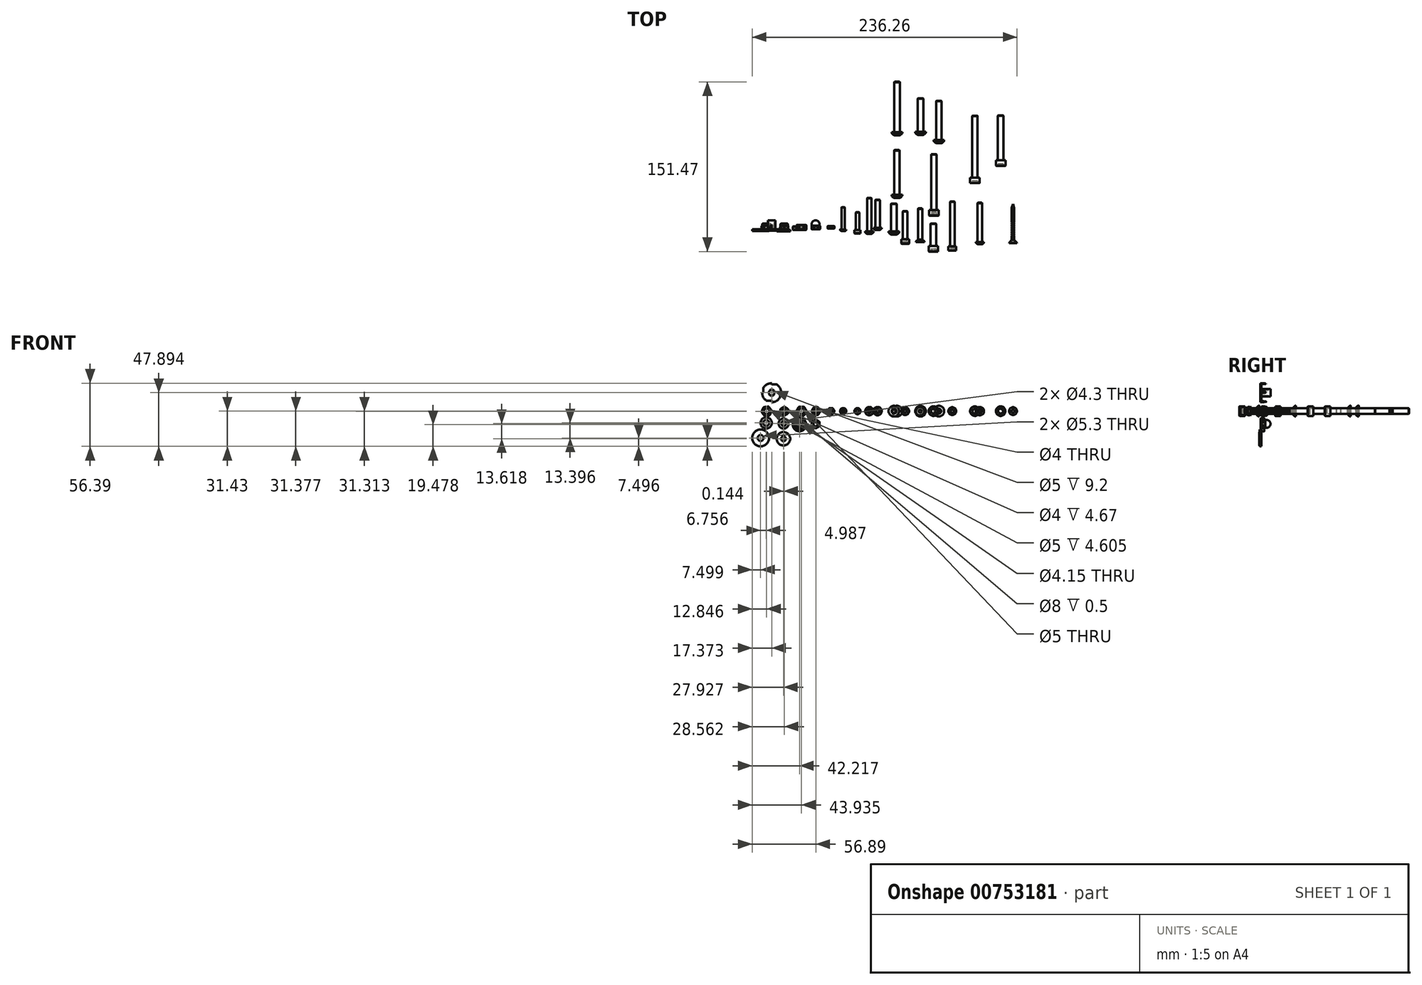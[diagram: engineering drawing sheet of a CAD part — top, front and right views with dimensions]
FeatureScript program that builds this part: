
annotation { "Feature Type Name" : "Feature", "Feature Type Description" : "" }
export const myFeature = defineFeature(function(context is Context, id is Id, definition is map)
    precondition{}
    {
        {
            var Q0;
            Q0=qCreatedBy(makeId("Top.planeOp"),FACE);
            var sketch = newSketch(context, id + "F0", { "sketchPlane" : qUnion([Q0])});
            skLineSegment(sketch, "E0.bottom", {"start": v(-2, 0) * mm, "end": v(-3.83, 0) * mm});
            skLineSegment(sketch, "E0.top", {"start": v(-2, 3) * mm, "end": v(-3.83, 3) * mm});
            skLineSegment(sketch, "E0.left", {"start": v(-2, 0) * mm, "end": v(-2, 3) * mm});
            skLineSegment(sketch, "E0.right", {"start": v(-3.83, 0) * mm, "end": v(-3.83, 3) * mm});
            skLineSegment(sketch, "E1", {"start": v(-2, 0) * mm, "end": v(0, 0) * mm, "construction": true});
            skLineSegment(sketch, "E2", {"start": v(0, 0) * mm, "end": v(0, 3) * mm, "construction": true});
            skSolve(sketch);
        }
        {
            var Q0;
            Q0=qSketchRegion(id+"F0",true);
            var Q1;
            Q1=sQuery(id+"F0.wireOp",EDGE,"E2");
            revolve(context, id + "F1", {"entities" : qUnion([Q0]), "axis" : qUnion([Q1]), "revolveType" : RevolveType.FULL});
        }
        {
            var Q0;
            Q0=makeQuery(id+"F1.opRevolve","SWEPT_EDGE",EDGE,{"disambiguationData":[OSD([sQuery(id+"F0.wireOp",EDGE,"E0.bottom"),sQuery(id+"F0.wireOp",EDGE,"E0.right")])]});
            var Q1;
            Q1=makeQuery(id+"F1.opRevolve","SWEPT_EDGE",EDGE,{"disambiguationData":[OSD([sQuery(id+"F0.wireOp",EDGE,"E0.top"),sQuery(id+"F0.wireOp",EDGE,"E0.right")])]});
            var Q2;
            Q2=makeQuery(id+"F1.opRevolve","SWEPT_EDGE",EDGE,{"disambiguationData":[OSD([sQuery(id+"F0.wireOp",EDGE,"E0.bottom"),sQuery(id+"F0.wireOp",EDGE,"E0.left")])]});
            var Q3;
            Q3=makeQuery(id+"F1.opRevolve","SWEPT_EDGE",EDGE,{"disambiguationData":[OSD([sQuery(id+"F0.wireOp",EDGE,"E0.top"),sQuery(id+"F0.wireOp",EDGE,"E0.left")])]});
            chamfer(context, id + "F2", {"entities" : qUnion([Q0, Q1, Q2, Q3]), "chamferType" : ChamferType.OFFSET_ANGLE, "width" : 0.77 * mm / 2, "oppositeDirection" : false, "angle" : 30 * degree, "tangentPropagation" : true});
        }
        {
            var Q0;
            Q0=makeQuery(id+"F1.opRevolve","SWEPT_FACE",FACE,{"disambiguationData":[OSD([sQuery(id+"F0.wireOp",EDGE,"E0.bottom")])]});
            var sketch = newSketch(context, id + "F3", { "sketchPlane" : qUnion([Q0])});
            skCircle(sketch, "E3.cCircle", {"center": v(0, 0) * mm, "radius": 3.45 * mm, "construction": true});
            skLineSegment(sketch, "E3.0", {"start": v(3.98, 0) * mm, "end": v(2, -3.45) * mm});
            skLineSegment(sketch, "E3.1", {"start": v(2, -3.45) * mm, "end": v(-2, -3.45) * mm});
            skLineSegment(sketch, "E3.2", {"start": v(-2, -3.45) * mm, "end": v(-3.98, 0) * mm});
            skLineSegment(sketch, "E3.3", {"start": v(-3.98, 0) * mm, "end": v(-2, 3.45) * mm});
            skLineSegment(sketch, "E3.4", {"start": v(-2, 3.45) * mm, "end": v(2, 3.45) * mm});
            skLineSegment(sketch, "E3.5", {"start": v(2, 3.45) * mm, "end": v(3.98, 0) * mm});
            skPoint(sketch, "E3.0.midPoint", {"position": v(2.99, -1.73) * mm});
            skCircle(sketch, "E4", {"center": v(0, 0) * mm, "radius": 4.53 * mm});
            skSolve(sketch);
        }
        {
            var Q0;
            Q0=qSketchRegion(id+"F3",true);
            extrude(context, id + "F4", {"entities" : qUnion([Q0]), "operationType" : NewBodyOperationType.REMOVE, "oppositeDirection" : true, "depth" : 25 * mm, "offsetDistance" : 25 * mm});
        }
        {
            var Q0;
            Q0=qCreatedBy(makeId("Top.planeOp"),FACE);
            var sketch = newSketch(context, id + "F5", { "sketchPlane" : qUnion([Q0])});
            skLineSegment(sketch, "E5.bottom", {"start": v(10.4, 2.85) * mm, "end": v(11.9, 2.85) * mm});
            skLineSegment(sketch, "E5.top", {"start": v(10.4, 0.58) * mm, "end": v(11.9, 0.58) * mm});
            skLineSegment(sketch, "E5.left", {"start": v(10.4, 2.85) * mm, "end": v(10.4, 0.58) * mm});
            skLineSegment(sketch, "E5.right", {"start": v(11.9, 2.85) * mm, "end": v(11.9, 0.58) * mm});
            skLineSegment(sketch, "E6", {"start": v(11.9, 0.58) * mm, "end": v(13.4, 0.58) * mm, "construction": true});
            skLineSegment(sketch, "E7", {"start": v(13.4, 0.58) * mm, "end": v(13.4, 2.85) * mm, "construction": true});
            skSolve(sketch);
        }
        {
            var Q0;
            Q0=qSketchRegion(id+"F5",true);
            var Q1;
            Q1=sQuery(id+"F5.wireOp",EDGE,"E7");
            revolve(context, id + "F6", {"entities" : qUnion([Q0]), "axis" : qUnion([Q1]), "revolveType" : RevolveType.FULL});
        }
        {
            var Q0;
            Q0=makeQuery(id+"F6.opRevolve","SWEPT_EDGE",EDGE,{"disambiguationData":[OSD([sQuery(id+"F5.wireOp",EDGE,"E5.top"),sQuery(id+"F5.wireOp",EDGE,"E5.right")])]});
            var Q1;
            Q1=makeQuery(id+"F6.opRevolve","SWEPT_EDGE",EDGE,{"disambiguationData":[OSD([sQuery(id+"F5.wireOp",EDGE,"E5.top"),sQuery(id+"F5.wireOp",EDGE,"E5.left")])]});
            var Q2;
            Q2=makeQuery(id+"F6.opRevolve","SWEPT_EDGE",EDGE,{"disambiguationData":[OSD([sQuery(id+"F5.wireOp",EDGE,"E5.bottom"),sQuery(id+"F5.wireOp",EDGE,"E5.right")])]});
            var Q3;
            Q3=makeQuery(id+"F6.opRevolve","SWEPT_EDGE",EDGE,{"disambiguationData":[OSD([sQuery(id+"F5.wireOp",EDGE,"E5.bottom"),sQuery(id+"F5.wireOp",EDGE,"E5.left")])]});
            chamfer(context, id + "F7", {"entities" : qUnion([Q0, Q1, Q2, Q3]), "width" : 0.51 / 2 * mm, "tangentPropagation" : true});
        }
        {
            var Q0;
            Q0=makeQuery(id+"F6.opRevolve","SWEPT_FACE",FACE,{"disambiguationData":[OSD([sQuery(id+"F5.wireOp",EDGE,"E5.top")])]});
            var sketch = newSketch(context, id + "F8", { "sketchPlane" : qUnion([Q0])});
            skCircle(sketch, "E8.cCircle", {"center": v(13.4, 0) * mm, "radius": 2.75 * mm, "construction": true});
            skLineSegment(sketch, "E8.0", {"start": v(16.58, 0) * mm, "end": v(15, -2.75) * mm});
            skLineSegment(sketch, "E8.1", {"start": v(15, -2.75) * mm, "end": v(11.82, -2.75) * mm});
            skLineSegment(sketch, "E8.2", {"start": v(11.82, -2.75) * mm, "end": v(10.23, 0) * mm});
            skLineSegment(sketch, "E8.3", {"start": v(10.23, 0) * mm, "end": v(11.82, 2.75) * mm});
            skLineSegment(sketch, "E8.4", {"start": v(11.82, 2.75) * mm, "end": v(15, 2.75) * mm});
            skLineSegment(sketch, "E8.5", {"start": v(15, 2.75) * mm, "end": v(16.58, 0) * mm});
            skPoint(sketch, "E8.0.midPoint", {"position": v(15.79, -1.38) * mm});
            skCircle(sketch, "E9", {"center": v(13.4, 0) * mm, "radius": 3.66 * mm});
            skSolve(sketch);
        }
        {
            var Q0;
            Q0=qSketchRegion(id+"F8",true);
            extrude(context, id + "F9", {"entities" : qUnion([Q0]), "operationType" : NewBodyOperationType.REMOVE, "oppositeDirection" : true, "depth" : 25 * mm, "offsetDistance" : 25 * mm});
        }
        {
            var Q0;
            Q0=qCreatedBy(makeId("Top.planeOp"),FACE);
            var sketch = newSketch(context, id + "F10", { "sketchPlane" : qUnion([Q0])});
            skLineSegment(sketch, "E10.bottom", {"start": v(-15.45, 3.8) * mm, "end": v(-17.35, 3.8) * mm});
            skLineSegment(sketch, "E10.top", {"start": v(-15.45, -0.05) * mm, "end": v(-17.35, -0.05) * mm});
            skLineSegment(sketch, "E10.left", {"start": v(-15.45, 3.8) * mm, "end": v(-15.45, -0.05) * mm});
            skLineSegment(sketch, "E10.right", {"start": v(-17.35, 3.8) * mm, "end": v(-17.35, -0.05) * mm});
            skLineSegment(sketch, "E11", {"start": v(-15.45, 3.8) * mm, "end": v(-12.95, 3.8) * mm, "construction": true});
            skLineSegment(sketch, "E12", {"start": v(-12.95, 3.8) * mm, "end": v(-12.95, -0.05) * mm, "construction": true});
            skSolve(sketch);
        }
        {
            var Q0;
            Q0=qSketchRegion(id+"F10",true);
            var Q1;
            Q1=sQuery(id+"F10.wireOp",EDGE,"E12");
            revolve(context, id + "F11", {"entities" : qUnion([Q0]), "axis" : qUnion([Q1]), "revolveType" : RevolveType.FULL});
        }
        {
            var Q0;
            Q0=makeQuery(id+"F11.opRevolve","SWEPT_EDGE",EDGE,{"disambiguationData":[OSD([sQuery(id+"F10.wireOp",EDGE,"E10.bottom"),sQuery(id+"F10.wireOp",EDGE,"E10.left")])]});
            var Q1;
            Q1=makeQuery(id+"F11.opRevolve","SWEPT_EDGE",EDGE,{"disambiguationData":[OSD([sQuery(id+"F10.wireOp",EDGE,"E10.bottom"),sQuery(id+"F10.wireOp",EDGE,"E10.right")])]});
            var Q2;
            Q2=makeQuery(id+"F11.opRevolve","SWEPT_EDGE",EDGE,{"disambiguationData":[OSD([sQuery(id+"F10.wireOp",EDGE,"E10.top"),sQuery(id+"F10.wireOp",EDGE,"E10.left")])]});
            var Q3;
            Q3=makeQuery(id+"F11.opRevolve","SWEPT_EDGE",EDGE,{"disambiguationData":[OSD([sQuery(id+"F10.wireOp",EDGE,"E10.top"),sQuery(id+"F10.wireOp",EDGE,"E10.right")])]});
            chamfer(context, id + "F12", {"entities" : qUnion([Q0, Q1, Q2, Q3]), "width" : 0.4 * mm, "tangentPropagation" : true});
        }
        {
            var Q0;
            Q0=makeQuery(id+"F11.opRevolve","SWEPT_FACE",FACE,{"disambiguationData":[OSD([sQuery(id+"F10.wireOp",EDGE,"E10.top")])]});
            var sketch = newSketch(context, id + "F13", { "sketchPlane" : qUnion([Q0])});
            skCircle(sketch, "E13.cCircle", {"center": v(-12.95, 0) * mm, "radius": 4 * mm, "construction": true});
            skLineSegment(sketch, "E13.0", {"start": v(-8.34, 0) * mm, "end": v(-10.65, -4) * mm});
            skLineSegment(sketch, "E13.1", {"start": v(-10.65, -4) * mm, "end": v(-15.26, -4) * mm});
            skLineSegment(sketch, "E13.2", {"start": v(-15.26, -4) * mm, "end": v(-17.57, 0) * mm});
            skLineSegment(sketch, "E13.3", {"start": v(-17.57, 0) * mm, "end": v(-15.26, 4) * mm});
            skLineSegment(sketch, "E13.4", {"start": v(-15.26, 4) * mm, "end": v(-10.65, 4) * mm});
            skLineSegment(sketch, "E13.5", {"start": v(-10.65, 4) * mm, "end": v(-8.34, 0) * mm});
            skPoint(sketch, "E13.0.midPoint", {"position": v(-9.5, -2) * mm});
            skCircle(sketch, "E14", {"center": v(-12.95, 0) * mm, "radius": 5.32 * mm});
            skSolve(sketch);
        }
        {
            var Q0;
            Q0=qSketchRegion(id+"F13",true);
            extrude(context, id + "F14", {"entities" : qUnion([Q0]), "operationType" : NewBodyOperationType.REMOVE, "oppositeDirection" : true, "depth" : 25 * mm, "offsetDistance" : 25 * mm});
        }
        {
            var Q0;
            Q0=qCreatedBy(makeId("Top.planeOp"),FACE);
            var sketch = newSketch(context, id + "F15", { "sketchPlane" : qUnion([Q0])});
            skLineSegment(sketch, "E15", {"start": v(24.32, 19.82) * mm, "end": v(24.32, -1.7) * mm});
            skLineSegment(sketch, "E16", {"start": v(24.32, -1.7) * mm, "end": v(22.95, -1.7) * mm});
            skLineSegment(sketch, "E17", {"start": v(21.55, -0.58) * mm, "end": v(21.55, -0.18) * mm});
            skLineSegment(sketch, "E18", {"start": v(21.55, -0.18) * mm, "end": v(22.82, -0.18) * mm});
            skLineSegment(sketch, "E19", {"start": v(22.82, -0.18) * mm, "end": v(22.82, 19.41) * mm});
            skLineSegment(sketch, "E20", {"start": v(22.82, 19.41) * mm, "end": v(23.18, 19.82) * mm});
            skLineSegment(sketch, "E21", {"start": v(23.18, 19.82) * mm, "end": v(24.32, 19.82) * mm});
            skArc(sketch, "E22", {"start": v(22.95, -1.7) * mm, "mid": v(22.16, -1.26) * mm, "end": v(21.55, -0.58) * mm});
            skSolve(sketch);
        }
        {
            var Q0;
            Q0=qSketchRegion(id+"F15",true);
            var Q1;
            Q1=sQuery(id+"F15.wireOp",EDGE,"E15");
            revolve(context, id + "F16", {"entities" : qUnion([Q0]), "axis" : qUnion([Q1]), "revolveType" : RevolveType.FULL});
        }
        {
            var Q0;
            Q0=makeQuery(id+"F16.opRevolve","SWEPT_FACE",FACE,{"disambiguationData":[OSD([sQuery(id+"F15.wireOp",EDGE,"E16")])]});
            var sketch = newSketch(context, id + "F17", { "sketchPlane" : qUnion([Q0])});
            skCircle(sketch, "E23.cCircle", {"center": v(24.32, 0) * mm, "radius": 1.02 * mm, "construction": true});
            skLineSegment(sketch, "E23.0", {"start": v(25.34, 0.59) * mm, "end": v(25.34, -0.59) * mm});
            skLineSegment(sketch, "E23.1", {"start": v(25.34, -0.59) * mm, "end": v(24.32, -1.17) * mm});
            skLineSegment(sketch, "E23.2", {"start": v(24.32, -1.17) * mm, "end": v(23.3, -0.59) * mm});
            skLineSegment(sketch, "E23.3", {"start": v(23.3, -0.59) * mm, "end": v(23.3, 0.59) * mm});
            skLineSegment(sketch, "E23.4", {"start": v(23.3, 0.59) * mm, "end": v(24.32, 1.17) * mm});
            skLineSegment(sketch, "E23.5", {"start": v(24.32, 1.17) * mm, "end": v(25.34, 0.59) * mm});
            skPoint(sketch, "E23.0.midPoint", {"position": v(25.34, 0) * mm});
            skSolve(sketch);
        }
        {
            var Q0;
            Q0=qSketchRegion(id+"F17",true);
            extrude(context, id + "F18", {"entities" : qUnion([Q0]), "operationType" : NewBodyOperationType.REMOVE, "oppositeDirection" : true, "depth" : 1.04 * mm, "offsetDistance" : 25 * mm});
        }
        {
            var Q0;
            Q0=qCreatedBy(makeId("Top.planeOp"),FACE);
            var sketch = newSketch(context, id + "F19", { "sketchPlane" : qUnion([Q0])});
            skLineSegment(sketch, "E24.bottom", {"start": v(34.33, -0.72) * mm, "end": v(35.58, -0.72) * mm});
            skLineSegment(sketch, "E24.top", {"start": v(34.61, -3.72) * mm, "end": v(37.08, -3.72) * mm});
            skLineSegment(sketch, "E24.left", {"start": v(34.33, -0.72) * mm, "end": v(34.33, -3.44) * mm});
            skLineSegment(sketch, "E24.right", {"start": v(37.08, -0.72) * mm, "end": v(37.08, -3.72) * mm});
            skLineSegment(sketch, "E25.top", {"start": v(37.08, 15.2) * mm, "end": v(35.86, 15.2) * mm});
            skLineSegment(sketch, "E25.left", {"start": v(37.08, -0.72) * mm, "end": v(37.08, 15.2) * mm});
            skLineSegment(sketch, "E25.right", {"start": v(35.58, -0.72) * mm, "end": v(35.58, 14.92) * mm});
            skLineSegment(sketch, "E26", {"start": v(34.33, -3.44) * mm, "end": v(34.61, -3.72) * mm});
            skLineSegment(sketch, "E27", {"start": v(35.58, 14.92) * mm, "end": v(35.86, 15.2) * mm});
            skSolve(sketch);
        }
        {
            var Q0;
            Q0=qSketchRegion(id+"F19",true);
            var Q1;
            Q1=sQuery(id+"F19.wireOp",EDGE,"E25.left");
            revolve(context, id + "F20", {"entities" : qUnion([Q0]), "axis" : qUnion([Q1]), "revolveType" : RevolveType.FULL});
        }
        {
            var Q0;
            Q0=makeQuery(id+"F20.opRevolve","SWEPT_FACE",FACE,{"disambiguationData":[OSD([sQuery(id+"F19.wireOp",EDGE,"E24.top")])]});
            var sketch = newSketch(context, id + "F21", { "sketchPlane" : qUnion([Q0])});
            skCircle(sketch, "E28.cCircle", {"center": v(37.08, 0) * mm, "radius": 1.25 * mm, "construction": true});
            skLineSegment(sketch, "E28.0", {"start": v(37.8, 1.25) * mm, "end": v(38.52, 0) * mm});
            skLineSegment(sketch, "E28.1", {"start": v(38.52, 0) * mm, "end": v(37.8, -1.25) * mm});
            skLineSegment(sketch, "E28.2", {"start": v(37.8, -1.25) * mm, "end": v(36.36, -1.25) * mm});
            skLineSegment(sketch, "E28.3", {"start": v(36.36, -1.25) * mm, "end": v(35.64, 0) * mm});
            skLineSegment(sketch, "E28.4", {"start": v(35.64, 0) * mm, "end": v(36.36, 1.25) * mm});
            skLineSegment(sketch, "E28.5", {"start": v(36.36, 1.25) * mm, "end": v(37.8, 1.25) * mm});
            skPoint(sketch, "E28.0.midPoint", {"position": v(38.16, 0.62) * mm});
            skSolve(sketch);
        }
        {
            var Q0;
            Q0=qSketchRegion(id+"F21",true);
            extrude(context, id + "F22", {"entities" : qUnion([Q0]), "operationType" : NewBodyOperationType.REMOVE, "oppositeDirection" : true, "depth" : 1.3 * mm, "offsetDistance" : 25 * mm});
        }
        {
            var Q0;
            Q0=qCreatedBy(makeId("Top.planeOp"),FACE);
            var sketch = newSketch(context, id + "F23", { "sketchPlane" : qUnion([Q0])});
            skLineSegment(sketch, "E29", {"start": v(55, 26.35) * mm, "end": v(55, -0.73) * mm});
            skLineSegment(sketch, "E30", {"start": v(55, -0.73) * mm, "end": v(53.25, -0.73) * mm});
            skLineSegment(sketch, "E31", {"start": v(51.3, 0.95) * mm, "end": v(51.3, 1.35) * mm});
            skLineSegment(sketch, "E32", {"start": v(51.3, 1.35) * mm, "end": v(53, 1.35) * mm});
            skLineSegment(sketch, "E33", {"start": v(53, 1.35) * mm, "end": v(53, 25.94) * mm});
            skLineSegment(sketch, "E34", {"start": v(53, 25.94) * mm, "end": v(53.36, 26.35) * mm});
            skLineSegment(sketch, "E35", {"start": v(53.36, 26.35) * mm, "end": v(55, 26.35) * mm});
            skArc(sketch, "E36", {"start": v(53.25, -0.73) * mm, "mid": v(52.07, -0.12) * mm, "end": v(51.3, 0.95) * mm});
            skSolve(sketch);
        }
        {
            var Q0;
            Q0=qSketchRegion(id+"F23",true);
            var Q1;
            Q1=sQuery(id+"F23.wireOp",EDGE,"E29");
            revolve(context, id + "F24", {"entities" : qUnion([Q0]), "axis" : qUnion([Q1]), "revolveType" : RevolveType.FULL});
        }
        {
            var Q0;
            Q0=makeQuery(id+"F24.opRevolve","SWEPT_FACE",FACE,{"disambiguationData":[OSD([sQuery(id+"F23.wireOp",EDGE,"E30")])]});
            var sketch = newSketch(context, id + "F25", { "sketchPlane" : qUnion([Q0])});
            skCircle(sketch, "E37.cCircle", {"center": v(55, 0) * mm, "radius": 1.27 * mm, "construction": true});
            skLineSegment(sketch, "E37.0", {"start": v(56.47, 0) * mm, "end": v(55.73, -1.27) * mm});
            skLineSegment(sketch, "E37.1", {"start": v(55.73, -1.27) * mm, "end": v(54.27, -1.27) * mm});
            skLineSegment(sketch, "E37.2", {"start": v(54.27, -1.27) * mm, "end": v(53.53, 0) * mm});
            skLineSegment(sketch, "E37.3", {"start": v(53.53, 0) * mm, "end": v(54.27, 1.27) * mm});
            skLineSegment(sketch, "E37.4", {"start": v(54.27, 1.27) * mm, "end": v(55.73, 1.27) * mm});
            skLineSegment(sketch, "E37.5", {"start": v(55.73, 1.27) * mm, "end": v(56.47, 0) * mm});
            skPoint(sketch, "E37.0.midPoint", {"position": v(56.1, -0.64) * mm});
            skSolve(sketch);
        }
        {
            var Q0;
            Q0=qSketchRegion(id+"F25",true);
            extrude(context, id + "F26", {"entities" : qUnion([Q0]), "operationType" : NewBodyOperationType.REMOVE, "oppositeDirection" : true, "depth" : 1.3 * mm, "offsetDistance" : 25 * mm});
        }
        {
            var Q0;
            Q0=qCreatedBy(makeId("Top.planeOp"),FACE);
            var sketch = newSketch(context, id + "F27", { "sketchPlane" : qUnion([Q0])});
            skLineSegment(sketch, "E38.bottom", {"start": v(76.11, -8.88) * mm, "end": v(77.61, -8.88) * mm});
            skLineSegment(sketch, "E38.top", {"start": v(76.4, -12.88) * mm, "end": v(79.61, -12.88) * mm});
            skLineSegment(sketch, "E38.left", {"start": v(76.11, -8.88) * mm, "end": v(76.11, -12.6) * mm});
            skLineSegment(sketch, "E38.right", {"start": v(79.61, -8.88) * mm, "end": v(79.61, -12.88) * mm});
            skLineSegment(sketch, "E39.top", {"start": v(79.61, 16.12) * mm, "end": v(77.9, 16.12) * mm});
            skLineSegment(sketch, "E39.left", {"start": v(79.61, -8.88) * mm, "end": v(79.61, 16.12) * mm});
            skLineSegment(sketch, "E39.right", {"start": v(77.61, -8.88) * mm, "end": v(77.61, 15.84) * mm});
            skLineSegment(sketch, "E40", {"start": v(76.11, -12.6) * mm, "end": v(76.4, -12.88) * mm});
            skLineSegment(sketch, "E41", {"start": v(77.61, 15.84) * mm, "end": v(77.9, 16.12) * mm});
            skSolve(sketch);
        }
        {
            var Q0;
            Q0=qSketchRegion(id+"F27",true);
            var Q1;
            Q1=sQuery(id+"F27.wireOp",EDGE,"E39.left");
            revolve(context, id + "F28", {"entities" : qUnion([Q0]), "axis" : qUnion([Q1]), "revolveType" : RevolveType.FULL});
        }
        {
            var Q0;
            Q0=makeQuery(id+"F28.opRevolve","SWEPT_FACE",FACE,{"disambiguationData":[OSD([sQuery(id+"F27.wireOp",EDGE,"E38.top")])]});
            var sketch = newSketch(context, id + "F29", { "sketchPlane" : qUnion([Q0])});
            skCircle(sketch, "E42.cCircle", {"center": v(79.61, 0) * mm, "radius": 1.5 * mm, "construction": true});
            skLineSegment(sketch, "E42.0", {"start": v(81.34, 0) * mm, "end": v(80.48, -1.5) * mm});
            skLineSegment(sketch, "E42.1", {"start": v(80.48, -1.5) * mm, "end": v(78.75, -1.5) * mm});
            skLineSegment(sketch, "E42.2", {"start": v(78.75, -1.5) * mm, "end": v(77.88, 0) * mm});
            skLineSegment(sketch, "E42.3", {"start": v(77.88, 0) * mm, "end": v(78.75, 1.5) * mm});
            skLineSegment(sketch, "E42.4", {"start": v(78.75, 1.5) * mm, "end": v(80.48, 1.5) * mm});
            skLineSegment(sketch, "E42.5", {"start": v(80.48, 1.5) * mm, "end": v(81.34, 0) * mm});
            skPoint(sketch, "E42.0.midPoint", {"position": v(80.91, -0.75) * mm});
            skSolve(sketch);
        }
        {
            var Q0;
            Q0=qSketchRegion(id+"F29",true);
            extrude(context, id + "F30", {"entities" : qUnion([Q0]), "operationType" : NewBodyOperationType.REMOVE, "oppositeDirection" : true, "depth" : 2 * mm, "offsetDistance" : 25 * mm});
        }
        {
            var Q0;
            Q0=qCreatedBy(makeId("Top.planeOp"),FACE);
            var sketch = newSketch(context, id + "F31", { "sketchPlane" : qUnion([Q0])});
            skLineSegment(sketch, "E43.bottom", {"start": v(100.55, -14.88) * mm, "end": v(102.3, -14.88) * mm});
            skLineSegment(sketch, "E43.top", {"start": v(100.83, -19.88) * mm, "end": v(104.8, -19.88) * mm});
            skLineSegment(sketch, "E43.left", {"start": v(100.55, -14.88) * mm, "end": v(100.55, -19.6) * mm});
            skLineSegment(sketch, "E43.right", {"start": v(104.8, -14.88) * mm, "end": v(104.8, -19.88) * mm});
            skLineSegment(sketch, "E44.top", {"start": v(104.8, 5.12) * mm, "end": v(102.58, 5.12) * mm});
            skLineSegment(sketch, "E44.left", {"start": v(104.8, -14.88) * mm, "end": v(104.8, 5.12) * mm});
            skLineSegment(sketch, "E44.right", {"start": v(102.3, -14.88) * mm, "end": v(102.3, 4.84) * mm});
            skLineSegment(sketch, "E45", {"start": v(100.55, -19.6) * mm, "end": v(100.83, -19.88) * mm});
            skLineSegment(sketch, "E46", {"start": v(102.3, 4.84) * mm, "end": v(102.58, 5.12) * mm});
            skSolve(sketch);
        }
        {
            var Q0;
            Q0=qSketchRegion(id+"F31",true);
            var Q1;
            Q1=sQuery(id+"F31.wireOp",EDGE,"E43.right");
            revolve(context, id + "F32", {"entities" : qUnion([Q0]), "axis" : qUnion([Q1]), "revolveType" : RevolveType.FULL});
        }
        {
            var Q0;
            Q0=makeQuery(id+"F32.opRevolve","SWEPT_FACE",FACE,{"disambiguationData":[OSD([sQuery(id+"F31.wireOp",EDGE,"E43.top")])]});
            var sketch = newSketch(context, id + "F33", { "sketchPlane" : qUnion([Q0])});
            skCircle(sketch, "E47.cCircle", {"center": v(104.8, 0) * mm, "radius": 2 * mm, "construction": true});
            skLineSegment(sketch, "E47.0", {"start": v(107.1, 0) * mm, "end": v(105.95, -2) * mm});
            skLineSegment(sketch, "E47.1", {"start": v(105.95, -2) * mm, "end": v(103.64, -2) * mm});
            skLineSegment(sketch, "E47.2", {"start": v(103.64, -2) * mm, "end": v(102.49, 0) * mm});
            skLineSegment(sketch, "E47.3", {"start": v(102.49, 0) * mm, "end": v(103.64, 2) * mm});
            skLineSegment(sketch, "E47.4", {"start": v(103.64, 2) * mm, "end": v(105.95, 2) * mm});
            skLineSegment(sketch, "E47.5", {"start": v(105.95, 2) * mm, "end": v(107.1, 0) * mm});
            skPoint(sketch, "E47.0.midPoint", {"position": v(106.53, -1) * mm});
            skSolve(sketch);
        }
        {
            var Q0;
            Q0=qSketchRegion(id+"F33",true);
            extrude(context, id + "F34", {"entities" : qUnion([Q0]), "operationType" : NewBodyOperationType.REMOVE, "oppositeDirection" : true, "depth" : 2.5 * mm, "offsetDistance" : 25 * mm});
        }
        {
            var Q0;
            Q0=qCreatedBy(makeId("Top.planeOp"),FACE);
            var sketch = newSketch(context, id + "F35", { "sketchPlane" : qUnion([Q0])});
            skLineSegment(sketch, "E48.bottom", {"start": v(118.16, -15.2) * mm, "end": v(119.66, -15.2) * mm});
            skLineSegment(sketch, "E48.top", {"start": v(118.45, -19.2) * mm, "end": v(121.66, -19.2) * mm});
            skLineSegment(sketch, "E48.left", {"start": v(118.16, -15.2) * mm, "end": v(118.16, -18.93) * mm});
            skLineSegment(sketch, "E48.right", {"start": v(121.66, -15.2) * mm, "end": v(121.66, -19.2) * mm});
            skLineSegment(sketch, "E49.top", {"start": v(121.66, 24.8) * mm, "end": v(119.95, 24.8) * mm});
            skLineSegment(sketch, "E49.left", {"start": v(121.66, -15.2) * mm, "end": v(121.66, 24.8) * mm});
            skLineSegment(sketch, "E49.right", {"start": v(119.66, -15.2) * mm, "end": v(119.66, 24.5) * mm});
            skLineSegment(sketch, "E50", {"start": v(118.16, -18.93) * mm, "end": v(118.45, -19.2) * mm});
            skLineSegment(sketch, "E51", {"start": v(119.66, 24.5) * mm, "end": v(119.95, 24.8) * mm});
            skSolve(sketch);
        }
        {
            var Q0;
            Q0=qSketchRegion(id+"F35",true);
            var Q1;
            Q1=sQuery(id+"F35.wireOp",EDGE,"E49.left");
            revolve(context, id + "F36", {"entities" : qUnion([Q0]), "axis" : qUnion([Q1]), "revolveType" : RevolveType.FULL});
        }
        {
            var Q0;
            Q0=makeQuery(id+"F36.opRevolve","SWEPT_FACE",FACE,{"disambiguationData":[OSD([sQuery(id+"F35.wireOp",EDGE,"E48.top")])]});
            var sketch = newSketch(context, id + "F37", { "sketchPlane" : qUnion([Q0])});
            skCircle(sketch, "E52.cCircle", {"center": v(121.66, 0) * mm, "radius": 1.5 * mm, "construction": true});
            skLineSegment(sketch, "E52.0", {"start": v(122.62, 1.44) * mm, "end": v(123.4, -0.1) * mm});
            skLineSegment(sketch, "E52.1", {"start": v(123.4, -0.1) * mm, "end": v(122.43, -1.55) * mm});
            skLineSegment(sketch, "E52.2", {"start": v(122.43, -1.55) * mm, "end": v(120.7, -1.44) * mm});
            skLineSegment(sketch, "E52.3", {"start": v(120.7, -1.44) * mm, "end": v(119.94, 0.1) * mm});
            skLineSegment(sketch, "E52.4", {"start": v(119.94, 0.1) * mm, "end": v(120.9, 1.55) * mm});
            skLineSegment(sketch, "E52.5", {"start": v(120.9, 1.55) * mm, "end": v(122.62, 1.44) * mm});
            skPoint(sketch, "E52.0.midPoint", {"position": v(123, 0.67) * mm});
            skSolve(sketch);
        }
        {
            var Q0;
            Q0=qSketchRegion(id+"F37",true);
            extrude(context, id + "F38", {"entities" : qUnion([Q0]), "operationType" : NewBodyOperationType.REMOVE, "oppositeDirection" : true, "depth" : 2.5 * mm, "offsetDistance" : 25 * mm});
        }
        {
            var Q0;
            Q0=qCreatedBy(makeId("Front.planeOp"),FACE);
            var sketch = newSketch(context, id + "F39", { "sketchPlane" : qUnion([Q0])});
            skCircle(sketch, "E53", {"center": v(-28.33, -0.05) * mm, "radius": 3.83 * mm});
            skCircle(sketch, "E54", {"center": v(-28.33, -0.05) * mm, "radius": 2 * mm});
            skSolve(sketch);
        }
        {
            var Q0;
            Q0=qSketchRegion(id+"F39",true);
            extrude(context, id + "F40", {"entities" : qUnion([Q0]), "oppositeDirection" : true, "depth" : 3.25 * mm, "offsetDistance" : 25 * mm});
        }
        {
            var Q0;
            Q0=makeQuery(id+"F40.opExtrude","CAP_EDGE",EDGE,{"disambiguationData":[OSD([sQuery(id+"F39.wireOp",EDGE,"E53")])],"isStart":false});
            var Q1;
            Q1=makeQuery(id+"F40.opExtrude","CAP_EDGE",EDGE,{"disambiguationData":[OSD([sQuery(id+"F39.wireOp",EDGE,"E53")])],"isStart":true});
            var Q2;
            Q2=makeQuery(id+"F40.opExtrude","CAP_EDGE",EDGE,{"disambiguationData":[OSD([sQuery(id+"F39.wireOp",EDGE,"E54")])],"isStart":true});
            chamfer(context, id + "F41", {"entities" : qUnion([Q0, Q1, Q2]), "width" : 0.66 / 2 * mm, "tangentPropagation" : true});
        }
        {
            var Q0;
            Q0=makeQuery(id+"F40.opExtrude","CAP_FACE",FACE,{"disambiguationData":[OSD([sQuery(id+"F39.wireOp",EDGE,"E53"),sQuery(id+"F39.wireOp",EDGE,"E54")])],"isStart":false});
            var sketch = newSketch(context, id + "F42", { "sketchPlane" : qUnion([Q0])});
            skCircle(sketch, "E55.cCircle", {"center": v(28.33, -0.05) * mm, "radius": 3.5 * mm, "construction": true});
            skLineSegment(sketch, "E55.0", {"start": v(31.83, 1.97) * mm, "end": v(31.83, -2.07) * mm});
            skLineSegment(sketch, "E55.1", {"start": v(31.83, -2.07) * mm, "end": v(28.33, -4.1) * mm});
            skLineSegment(sketch, "E55.2", {"start": v(28.33, -4.1) * mm, "end": v(24.83, -2.07) * mm});
            skLineSegment(sketch, "E55.3", {"start": v(24.83, -2.07) * mm, "end": v(24.83, 1.97) * mm});
            skLineSegment(sketch, "E55.4", {"start": v(24.83, 1.97) * mm, "end": v(28.33, 3.99) * mm});
            skLineSegment(sketch, "E55.5", {"start": v(28.33, 3.99) * mm, "end": v(31.83, 1.97) * mm});
            skPoint(sketch, "E55.0.midPoint", {"position": v(31.83, -0.05) * mm});
            skCircle(sketch, "E56", {"center": v(28.33, -0.05) * mm, "radius": 6.48 * mm});
            skSolve(sketch);
        }
        {
            var Q0;
            Q0=qSketchRegion(id+"F42",true);
            extrude(context, id + "F43", {"entities" : qUnion([Q0]), "operationType" : NewBodyOperationType.REMOVE, "oppositeDirection" : true, "depth" : 25 * mm, "offsetDistance" : 25 * mm});
        }
        {
            var Q0;
            Q0=makeQuery(id+"F40.opExtrude","CAP_FACE",FACE,{"disambiguationData":[OSD([sQuery(id+"F39.wireOp",EDGE,"E53"),sQuery(id+"F39.wireOp",EDGE,"E54")])],"isStart":false});
            var sketch = newSketch(context, id + "F44", { "sketchPlane" : qUnion([Q0])});
            skCircle(sketch, "E57", {"center": v(28.33, -0.05) * mm, "radius": 2 * mm});
            skCircle(sketch, "E58", {"center": v(28.33, -0.05) * mm, "radius": 3.38 * mm});
            skSolve(sketch);
        }
        {
            var Q0;
            Q0=qSketchRegion(id+"F44",true);
            extrude(context, id + "F45", {"entities" : qUnion([Q0]), "operationType" : NewBodyOperationType.ADD, "depth" : (5 - 3.25) * mm, "offsetDistance" : 25 * mm});
        }
        {
            var Q0;
            Q0=makeQuery(id+"F45.opExtrude","CAP_EDGE",EDGE,{"disambiguationData":[OSD([sQuery(id+"F44.wireOp",EDGE,"E58")])],"isStart":false});
            fillet(context, id + "F46", {"entities" : qUnion([Q0]), "radius" : 0.75 * mm, "tangentPropagation" : true, "allowEdgeOverflow" : false});
        }
        {
            var Q0;
            Q0=qCreatedBy(makeId("Top.planeOp"),FACE);
            var sketch = newSketch(context, id + "F47", { "sketchPlane" : qUnion([Q0])});
            skLineSegment(sketch, "E59", {"start": v(69.58, 22.98) * mm, "end": v(69.58, -4.77) * mm});
            skLineSegment(sketch, "E60", {"start": v(69.58, -4.77) * mm, "end": v(67.48, -4.77) * mm});
            skLineSegment(sketch, "E61", {"start": v(64.83, -2.62) * mm, "end": v(64.83, -2.02) * mm});
            skLineSegment(sketch, "E62", {"start": v(64.83, -2.02) * mm, "end": v(67.08, -2.02) * mm});
            skLineSegment(sketch, "E63", {"start": v(67.08, -2.02) * mm, "end": v(67.08, 22.58) * mm});
            skLineSegment(sketch, "E64", {"start": v(67.08, 22.58) * mm, "end": v(67.44, 22.98) * mm});
            skLineSegment(sketch, "E65", {"start": v(67.44, 22.98) * mm, "end": v(69.58, 22.98) * mm});
            skArc(sketch, "E66", {"start": v(67.48, -4.77) * mm, "mid": v(65.88, -4.03) * mm, "end": v(64.83, -2.62) * mm});
            skSolve(sketch);
        }
        {
            var Q0;
            Q0=makeQuery(id+"F47.imprint","IMPRINT",FACE,{"disambiguationData":[TD([[makeQuery(id+"F47.imprint","IMPRINT",EDGE,{"derivedFrom":sQuery(id+"F47.wireOp",EDGE,"E59")}),-1.0]])]});
            var Q1;
            Q1=sQuery(id+"F47.wireOp",EDGE,"E59");
            revolve(context, id + "F48", {"entities" : qUnion([Q0]), "axis" : qUnion([Q1]), "revolveType" : RevolveType.FULL});
        }
        {
            var Q0;
            Q0=makeQuery(id+"F48.opRevolve","SWEPT_FACE",FACE,{"disambiguationData":[OSD([sQuery(id+"F47.wireOp",EDGE,"E60")])]});
            var sketch = newSketch(context, id + "F49", { "sketchPlane" : qUnion([Q0])});
            skCircle(sketch, "E67.cCircle", {"center": v(69.58, 0) * mm, "radius": 1.5 * mm, "construction": true});
            skLineSegment(sketch, "E67.0", {"start": v(69.92, 1.7) * mm, "end": v(71.22, 0.55) * mm});
            skLineSegment(sketch, "E67.1", {"start": v(71.22, 0.55) * mm, "end": v(70.88, -1.14) * mm});
            skLineSegment(sketch, "E67.2", {"start": v(70.88, -1.14) * mm, "end": v(69.24, -1.7) * mm});
            skLineSegment(sketch, "E67.3", {"start": v(69.24, -1.7) * mm, "end": v(67.94, -0.55) * mm});
            skLineSegment(sketch, "E67.4", {"start": v(67.94, -0.55) * mm, "end": v(68.28, 1.14) * mm});
            skLineSegment(sketch, "E67.5", {"start": v(68.28, 1.14) * mm, "end": v(69.92, 1.7) * mm});
            skPoint(sketch, "E67.0.midPoint", {"position": v(70.57, 1.13) * mm});
            skSolve(sketch);
        }
        {
            var Q0;
            Q0=qSketchRegion(id+"F49",true);
            extrude(context, id + "F50", {"entities" : qUnion([Q0]), "operationType" : NewBodyOperationType.REMOVE, "oppositeDirection" : true, "depth" : 1.56 * mm, "offsetDistance" : 25 * mm});
        }
        {
            var Q0;
            Q0=qCreatedBy(makeId("Front.planeOp"),FACE);
            var sketch = newSketch(context, id + "F51", { "sketchPlane" : qUnion([Q0])});
            skCircle(sketch, "E68", {"center": v(-44.04, -0.12) * mm, "radius": 4.4 * mm});
            skCircle(sketch, "E69", {"center": v(-44.04, -0.12) * mm, "radius": 2.5 * mm});
            skSolve(sketch);
        }
        {
            var Q0;
            Q0=qSketchRegion(id+"F51",true);
            extrude(context, id + "F52", {"entities" : qUnion([Q0]), "oppositeDirection" : true, "depth" : 3.25 * mm, "offsetDistance" : 25 * mm});
        }
        {
            var Q0;
            Q0=makeQuery(id+"F52.opExtrude","CAP_EDGE",EDGE,{"disambiguationData":[OSD([sQuery(id+"F51.wireOp",EDGE,"E68")])],"isStart":false});
            var Q1;
            Q1=makeQuery(id+"F52.opExtrude","CAP_EDGE",EDGE,{"disambiguationData":[OSD([sQuery(id+"F51.wireOp",EDGE,"E68")])],"isStart":true});
            var Q2;
            Q2=makeQuery(id+"F52.opExtrude","CAP_EDGE",EDGE,{"disambiguationData":[OSD([sQuery(id+"F51.wireOp",EDGE,"E69")])],"isStart":true});
            chamfer(context, id + "F53", {"entities" : qUnion([Q0, Q1, Q2]), "width" : (0.79 / 2) * mm, "tangentPropagation" : true});
        }
        {
            var Q0;
            Q0=makeQuery(id+"F52.opExtrude","CAP_FACE",FACE,{"disambiguationData":[OSD([sQuery(id+"F51.wireOp",EDGE,"E68"),sQuery(id+"F51.wireOp",EDGE,"E69")])],"isStart":false});
            var sketch = newSketch(context, id + "F54", { "sketchPlane" : qUnion([Q0])});
            skCircle(sketch, "E70.cCircle", {"center": v(44.04, -0.12) * mm, "radius": 4 * mm, "construction": true});
            skLineSegment(sketch, "E70.0", {"start": v(39.46, 0.47) * mm, "end": v(42.26, 4.14) * mm});
            skLineSegment(sketch, "E70.1", {"start": v(42.26, 4.14) * mm, "end": v(46.84, 3.56) * mm});
            skLineSegment(sketch, "E70.2", {"start": v(46.84, 3.56) * mm, "end": v(48.63, -0.7) * mm});
            skLineSegment(sketch, "E70.3", {"start": v(48.63, -0.7) * mm, "end": v(45.83, -4.38) * mm});
            skLineSegment(sketch, "E70.4", {"start": v(45.83, -4.38) * mm, "end": v(41.25, -3.8) * mm});
            skLineSegment(sketch, "E70.5", {"start": v(41.25, -3.8) * mm, "end": v(39.46, 0.47) * mm});
            skPoint(sketch, "E70.0.midPoint", {"position": v(40.86, 2.3) * mm});
            skCircle(sketch, "E71", {"center": v(44.04, -0.12) * mm, "radius": 6.63 * mm});
            skSolve(sketch);
        }
        {
            var Q0;
            Q0=qSketchRegion(id+"F54",true);
            extrude(context, id + "F55", {"entities" : qUnion([Q0]), "operationType" : NewBodyOperationType.REMOVE, "oppositeDirection" : true, "depth" : 25 * mm, "offsetDistance" : 25 * mm});
        }
        {
            var Q0;
            Q0=makeQuery(id+"F52.opExtrude","CAP_FACE",FACE,{"disambiguationData":[OSD([sQuery(id+"F51.wireOp",EDGE,"E68"),sQuery(id+"F51.wireOp",EDGE,"E69")])],"isStart":false});
            var sketch = newSketch(context, id + "F56", { "sketchPlane" : qUnion([Q0])});
            skCircle(sketch, "E72", {"center": v(44.04, -0.12) * mm, "radius": 2.5 * mm});
            skCircle(sketch, "E73", {"center": v(44.04, -0.12) * mm, "radius": 3.88 * mm});
            skSolve(sketch);
        }
        {
            var Q0;
            Q0=qSketchRegion(id+"F56",true);
            extrude(context, id + "F57", {"entities" : qUnion([Q0]), "operationType" : NewBodyOperationType.ADD, "depth" : 1.75 * mm, "offsetDistance" : 25 * mm});
        }
        {
            var Q0;
            Q0=makeQuery(id+"F57.opExtrude","CAP_EDGE",EDGE,{"disambiguationData":[OSD([sQuery(id+"F56.wireOp",EDGE,"E73")])],"isStart":false});
            fillet(context, id + "F58", {"entities" : qUnion([Q0]), "radius" : 0.75 * mm, "tangentPropagation" : true, "allowEdgeOverflow" : false});
        }
        {
            var Q0;
            Q0=qCreatedBy(makeId("Front.planeOp"),FACE);
            var sketch = newSketch(context, id + "F59", { "sketchPlane" : qUnion([Q0])});
            skCircle(sketch, "E74", {"center": v(-44.4, -10.54) * mm, "radius": 2.65 * mm});
            skCircle(sketch, "E75", {"center": v(-44.4, -10.54) * mm, "radius": 5 * mm});
            skSolve(sketch);
        }
        {
            var Q0;
            Q0=qSketchRegion(id+"F59",true);
            extrude(context, id + "F60", {"entities" : qUnion([Q0]), "oppositeDirection" : true, "depth" : 1 * mm, "offsetDistance" : 25 * mm});
        }
        {
            var Q0;
            Q0=qCreatedBy(makeId("Top.planeOp"),FACE);
            var sketch = newSketch(context, id + "F61", { "sketchPlane" : qUnion([Q0])});
            skLineSegment(sketch, "E76", {"start": v(47.6, 27.95) * mm, "end": v(47.6, -4.13) * mm});
            skLineSegment(sketch, "E77", {"start": v(47.6, -4.13) * mm, "end": v(45.86, -4.13) * mm});
            skLineSegment(sketch, "E78", {"start": v(43.9, -2.45) * mm, "end": v(43.9, -2.05) * mm});
            skLineSegment(sketch, "E79", {"start": v(43.9, -2.05) * mm, "end": v(45.6, -2.05) * mm});
            skLineSegment(sketch, "E80", {"start": v(45.6, -2.05) * mm, "end": v(45.6, 27.54) * mm});
            skLineSegment(sketch, "E81", {"start": v(45.6, 27.54) * mm, "end": v(45.97, 27.95) * mm});
            skLineSegment(sketch, "E82", {"start": v(45.97, 27.95) * mm, "end": v(47.6, 27.95) * mm});
            skArc(sketch, "E83", {"start": v(45.86, -4.13) * mm, "mid": v(44.68, -3.53) * mm, "end": v(43.9, -2.45) * mm});
            skSolve(sketch);
        }
        {
            var Q0;
            Q0=makeQuery(id+"F61.imprint","IMPRINT",FACE,{"disambiguationData":[TD([[makeQuery(id+"F61.imprint","IMPRINT",EDGE,{"derivedFrom":sQuery(id+"F61.wireOp",EDGE,"E76")}),-1.0]])]});
            var Q1;
            Q1=sQuery(id+"F61.wireOp",EDGE,"E76");
            revolve(context, id + "F62", {"entities" : qUnion([Q0]), "axis" : qUnion([Q1]), "revolveType" : RevolveType.FULL});
        }
        {
            var Q0;
            Q0=makeQuery(id+"F62.opRevolve","SWEPT_FACE",FACE,{"disambiguationData":[OSD([sQuery(id+"F61.wireOp",EDGE,"E77")])]});
            var sketch = newSketch(context, id + "F63", { "sketchPlane" : qUnion([Q0])});
            skCircle(sketch, "E84.cCircle", {"center": v(47.6, 0) * mm, "radius": 1.25 * mm, "construction": true});
            skLineSegment(sketch, "E84.0", {"start": v(48.97, -0.48) * mm, "end": v(47.87, -1.42) * mm});
            skLineSegment(sketch, "E84.1", {"start": v(47.87, -1.42) * mm, "end": v(46.51, -0.94) * mm});
            skLineSegment(sketch, "E84.2", {"start": v(46.51, -0.94) * mm, "end": v(46.25, 0.48) * mm});
            skLineSegment(sketch, "E84.3", {"start": v(46.25, 0.48) * mm, "end": v(47.35, 1.42) * mm});
            skLineSegment(sketch, "E84.4", {"start": v(47.35, 1.42) * mm, "end": v(48.7, 0.94) * mm});
            skLineSegment(sketch, "E84.5", {"start": v(48.7, 0.94) * mm, "end": v(48.97, -0.48) * mm});
            skPoint(sketch, "E84.0.midPoint", {"position": v(48.42, -0.95) * mm});
            skSolve(sketch);
        }
        {
            var Q0;
            Q0=qSketchRegion(id+"F63",true);
            extrude(context, id + "F64", {"entities" : qUnion([Q0]), "operationType" : NewBodyOperationType.REMOVE, "oppositeDirection" : true, "depth" : 1.3 * mm, "offsetDistance" : 25 * mm});
        }
        {
            var Q0;
            Q0=qCreatedBy(makeId("Front.planeOp"),FACE);
            var sketch = newSketch(context, id + "F65", { "sketchPlane" : qUnion([Q0])});
            skCircle(sketch, "E85", {"center": v(-28.82, -11.06) * mm, "radius": 2.15 * mm});
            skCircle(sketch, "E86", {"center": v(-28.82, -11.06) * mm, "radius": 4.5 * mm});
            skSolve(sketch);
        }
        {
            var Q0;
            Q0=qSketchRegion(id+"F65",true);
            extrude(context, id + "F66", {"entities" : qUnion([Q0]), "depth" : 0.8 * mm, "offsetDistance" : 25 * mm});
        }
        {
            var Q0;
            Q0=qCreatedBy(makeId("Front.planeOp"),FACE);
            var sketch = newSketch(context, id + "F67", { "sketchPlane" : qUnion([Q0])});
            skCircle(sketch, "E87", {"center": v(-0.33, -11.42) * mm, "radius": 3.83 * mm});
            skCircle(sketch, "E88", {"center": v(-0.33, -11.42) * mm, "radius": 2 * mm});
            skSolve(sketch);
        }
        {
            var Q0;
            Q0=qSketchRegion(id+"F67",true);
            extrude(context, id + "F68", {"entities" : qUnion([Q0]), "oppositeDirection" : true, "depth" : 3.25 * mm, "offsetDistance" : 25 * mm});
        }
        {
            var Q0;
            Q0=makeQuery(id+"F68.opExtrude","CAP_EDGE",EDGE,{"disambiguationData":[OSD([sQuery(id+"F67.wireOp",EDGE,"E87")])],"isStart":true});
            var Q1;
            Q1=makeQuery(id+"F68.opExtrude","CAP_EDGE",EDGE,{"disambiguationData":[OSD([sQuery(id+"F67.wireOp",EDGE,"E88")])],"isStart":true});
            var Q2;
            Q2=makeQuery(id+"F68.opExtrude","CAP_EDGE",EDGE,{"disambiguationData":[OSD([sQuery(id+"F67.wireOp",EDGE,"E87")])],"isStart":false});
            chamfer(context, id + "F69", {"entities" : qUnion([Q0, Q1, Q2]), "width" : 0.33 * mm, "tangentPropagation" : true});
        }
        {
            var Q0;
            Q0=makeQuery(id+"F68.opExtrude","CAP_FACE",FACE,{"disambiguationData":[OSD([sQuery(id+"F67.wireOp",EDGE,"E87"),sQuery(id+"F67.wireOp",EDGE,"E88")])],"isStart":false});
            var sketch = newSketch(context, id + "F70", { "sketchPlane" : qUnion([Q0])});
            skCircle(sketch, "E89", {"center": v(0.33, -11.42) * mm, "radius": 3.5 * mm});
            skSolve(sketch);
        }
        {
            var Q0;
            Q0=qSketchRegion(id+"F70",true);
            extrude(context, id + "F71", {"entities" : qUnion([Q0]), "operationType" : NewBodyOperationType.ADD, "depth" : 4.75 * mm, "offsetDistance" : 25 * mm});
        }
        {
            var Q0;
            Q0=makeQuery(id+"F71.opExtrude","CAP_EDGE",EDGE,{"disambiguationData":[OSD([sQuery(id+"F70.wireOp",EDGE,"E89")])],"isStart":false});
            fillet(context, id + "F72", {"entities" : qUnion([Q0]), "radius" : 3.5 * mm, "tangentPropagation" : true, "allowEdgeOverflow" : false});
        }
        {
            var Q0;
            Q0=makeQuery(id+"F68.opExtrude","CAP_FACE",FACE,{"disambiguationData":[OSD([sQuery(id+"F67.wireOp",EDGE,"E87"),sQuery(id+"F67.wireOp",EDGE,"E88")])],"isStart":true});
            var sketch = newSketch(context, id + "F73", { "sketchPlane" : qUnion([Q0])});
            skCircle(sketch, "E90.cCircle", {"center": v(-0.33, -11.42) * mm, "radius": 3.5 * mm, "construction": true});
            skLineSegment(sketch, "E90.0", {"start": v(3.17, -9.4) * mm, "end": v(3.17, -13.44) * mm});
            skLineSegment(sketch, "E90.1", {"start": v(3.17, -13.44) * mm, "end": v(-0.33, -15.47) * mm});
            skLineSegment(sketch, "E90.2", {"start": v(-0.33, -15.47) * mm, "end": v(-3.83, -13.44) * mm});
            skLineSegment(sketch, "E90.3", {"start": v(-3.83, -13.44) * mm, "end": v(-3.83, -9.4) * mm});
            skLineSegment(sketch, "E90.4", {"start": v(-3.83, -9.4) * mm, "end": v(-0.33, -7.38) * mm});
            skLineSegment(sketch, "E90.5", {"start": v(-0.33, -7.38) * mm, "end": v(3.17, -9.4) * mm});
            skPoint(sketch, "E90.0.midPoint", {"position": v(3.17, -11.42) * mm});
            skCircle(sketch, "E91", {"center": v(-0.33, -11.42) * mm, "radius": 6.02 * mm});
            skSolve(sketch);
        }
        {
            var Q0;
            Q0=qSketchRegion(id+"F73",true);
            extrude(context, id + "F74", {"entities" : qUnion([Q0]), "operationType" : NewBodyOperationType.REMOVE, "oppositeDirection" : true, "depth" : 25 * mm, "offsetDistance" : 25 * mm});
        }
        {
            var Q0;
            Q0=qCreatedBy(makeId("Front.planeOp"),FACE);
            var sketch = newSketch(context, id + "F75", { "sketchPlane" : qUnion([Q0])});
            skCircle(sketch, "E92", {"center": v(-14.67, -11.95) * mm, "radius": 6 * mm});
            skCircle(sketch, "E93", {"center": v(-14.67, -11.95) * mm, "radius": 2.08 * mm});
            skSolve(sketch);
        }
        {
            var Q0;
            Q0=qSketchRegion(id+"F75",true);
            extrude(context, id + "F76", {"entities" : qUnion([Q0]), "depth" : 0.5 * mm, "offsetDistance" : 25 * mm, "hasSecondDirection" : true, "secondDirectionOppositeDirection" : true, "secondDirectionDepth" : 2.5 * mm});
        }
        {
            var Q0;
            Q0=qCreatedBy(makeId("Front.planeOp"),FACE);
            var sketch = newSketch(context, id + "F77", { "sketchPlane" : qUnion([Q0])});
            skCircle(sketch, "E94", {"center": v(-14.67, -11.95) * mm, "radius": 4 * mm});
            skSolve(sketch);
        }
        {
            var Q0;
            Q0=qSketchRegion(id+"F77",true);
            extrude(context, id + "F78", {"entities" : qUnion([Q0]), "operationType" : NewBodyOperationType.REMOVE, "oppositeDirection" : true, "depth" : 25 * mm, "offsetDistance" : 25 * mm, "hasDraft" : true, "draftAngle" : 45 * degree, "draftPullDirection" : true, "hasSecondDirection" : true, "secondDirectionOppositeDirection" : false, "secondDirectionDepth" : 25 * mm});
        }
        {
            var Q0;
            Q0=makeQuery(id+"F76.opExtrude","CAP_EDGE",EDGE,{"disambiguationData":[OSD([sQuery(id+"F75.wireOp",EDGE,"E92")])],"isStart":false});
            var Q1;
            Q1=makeQuery(id+"F76.opExtrude","CAP_EDGE",EDGE,{"disambiguationData":[OSD([sQuery(id+"F75.wireOp",EDGE,"E92")])],"isStart":true});
            chamfer(context, id + "F79", {"entities" : qUnion([Q0, Q1]), "width" : 0.2 * mm, "tangentPropagation" : true});
        }
        {
            var Q0;
            Q0=qCreatedBy(makeId("Top.planeOp"),FACE);
            var sketch = newSketch(context, id + "F80", { "sketchPlane" : qUnion([Q0])});
            skLineSegment(sketch, "E95", {"start": v(93, -11.43) * mm, "end": v(89.2, -11.43) * mm});
            skLineSegment(sketch, "E96", {"start": v(89.2, -11.43) * mm, "end": v(89.2, -10.93) * mm});
            skLineSegment(sketch, "E97", {"start": v(89.2, -10.93) * mm, "end": v(91, -9.13) * mm});
            skLineSegment(sketch, "E98", {"start": v(91, -9.13) * mm, "end": v(91, 18.22) * mm});
            skLineSegment(sketch, "E99", {"start": v(91, 18.22) * mm, "end": v(91.36, 18.57) * mm});
            skLineSegment(sketch, "E100", {"start": v(91.36, 18.57) * mm, "end": v(93, 18.57) * mm});
            skLineSegment(sketch, "E101", {"start": v(93, 18.57) * mm, "end": v(93, -11.43) * mm});
            skSolve(sketch);
        }
        {
            var Q0;
            Q0=qSketchRegion(id+"F80",true);
            var Q1;
            Q1=sQuery(id+"F80.wireOp",EDGE,"E101");
            revolve(context, id + "F81", {"entities" : qUnion([Q0]), "axis" : qUnion([Q1]), "revolveType" : RevolveType.FULL});
        }
        {
            var Q0;
            Q0=makeQuery(id+"F81.opRevolve","SWEPT_FACE",FACE,{"disambiguationData":[OSD([sQuery(id+"F80.wireOp",EDGE,"E95")])]});
            var sketch = newSketch(context, id + "F82", { "sketchPlane" : qUnion([Q0])});
            skCircle(sketch, "E102.cCircle", {"center": v(93, 0) * mm, "radius": 1.25 * mm, "construction": true});
            skLineSegment(sketch, "E102.0", {"start": v(92.74, 1.42) * mm, "end": v(94.1, 0.94) * mm});
            skLineSegment(sketch, "E102.1", {"start": v(94.1, 0.94) * mm, "end": v(94.36, -0.48) * mm});
            skLineSegment(sketch, "E102.2", {"start": v(94.36, -0.48) * mm, "end": v(93.27, -1.42) * mm});
            skLineSegment(sketch, "E102.3", {"start": v(93.27, -1.42) * mm, "end": v(91.9, -0.94) * mm});
            skLineSegment(sketch, "E102.4", {"start": v(91.9, -0.94) * mm, "end": v(91.64, 0.48) * mm});
            skLineSegment(sketch, "E102.5", {"start": v(91.64, 0.48) * mm, "end": v(92.74, 1.42) * mm});
            skPoint(sketch, "E102.0.midPoint", {"position": v(93.42, 1.18) * mm});
            skSolve(sketch);
        }
        {
            var Q0;
            Q0=qSketchRegion(id+"F82",true);
            extrude(context, id + "F83", {"entities" : qUnion([Q0]), "operationType" : NewBodyOperationType.REMOVE, "oppositeDirection" : true, "depth" : 1.8 * mm, "offsetDistance" : 25 * mm});
        }
        {
            var Q0;
            Q0=qCreatedBy(makeId("Top.planeOp"),FACE);
            var sketch = newSketch(context, id + "F84", { "sketchPlane" : qUnion([Q0])});
            skLineSegment(sketch, "E103", {"start": v(146.3, 23.7) * mm, "end": v(146.3, -13.38) * mm});
            skLineSegment(sketch, "E104", {"start": v(146.3, -13.38) * mm, "end": v(144.56, -13.38) * mm});
            skLineSegment(sketch, "E105", {"start": v(142.6, -11.7) * mm, "end": v(142.6, -11.3) * mm});
            skLineSegment(sketch, "E106", {"start": v(142.6, -11.3) * mm, "end": v(144.3, -11.3) * mm});
            skLineSegment(sketch, "E107", {"start": v(144.3, -11.3) * mm, "end": v(144.3, 23.3) * mm});
            skLineSegment(sketch, "E108", {"start": v(144.3, 23.3) * mm, "end": v(144.67, 23.7) * mm});
            skLineSegment(sketch, "E109", {"start": v(144.67, 23.7) * mm, "end": v(146.3, 23.7) * mm});
            skArc(sketch, "E110", {"start": v(144.56, -13.38) * mm, "mid": v(143.38, -12.78) * mm, "end": v(142.6, -11.7) * mm});
            skSolve(sketch);
        }
        {
            var Q0;
            Q0=qSketchRegion(id+"F84",true);
            var Q1;
            Q1=sQuery(id+"F84.wireOp",EDGE,"E103");
            revolve(context, id + "F85", {"surfaceOperationType" : NewSurfaceOperationType.NEW, "entities" : qUnion([Q0]), "axis" : qUnion([Q1]), "revolveType" : RevolveType.FULL});
        }
        {
            var Q0;
            Q0=makeQuery(id+"F85.opRevolve","SWEPT_FACE",FACE,{"disambiguationData":[OSD([sQuery(id+"F84.wireOp",EDGE,"E104")])]});
            var sketch = newSketch(context, id + "F86", { "sketchPlane" : qUnion([Q0])});
            skCircle(sketch, "E111.cCircle", {"center": v(146.3, 0) * mm, "radius": 1.25 * mm, "construction": true});
            skLineSegment(sketch, "E111.0", {"start": v(147.75, 0.08) * mm, "end": v(147.1, -1.2) * mm});
            skLineSegment(sketch, "E111.1", {"start": v(147.1, -1.2) * mm, "end": v(145.66, -1.29) * mm});
            skLineSegment(sketch, "E111.2", {"start": v(145.66, -1.29) * mm, "end": v(144.87, -0.08) * mm});
            skLineSegment(sketch, "E111.3", {"start": v(144.87, -0.08) * mm, "end": v(145.52, 1.2) * mm});
            skLineSegment(sketch, "E111.4", {"start": v(145.52, 1.2) * mm, "end": v(146.96, 1.29) * mm});
            skLineSegment(sketch, "E111.5", {"start": v(146.96, 1.29) * mm, "end": v(147.75, 0.08) * mm});
            skPoint(sketch, "E111.0.midPoint", {"position": v(147.43, -0.56) * mm});
            skSolve(sketch);
        }
        {
            var Q0;
            Q0=qSketchRegion(id+"F86",true);
            extrude(context, id + "F87", {"entities" : qUnion([Q0]), "operationType" : NewBodyOperationType.REMOVE, "oppositeDirection" : true, "depth" : 2 * mm, "offsetDistance" : 25 * mm});
        }
        {
            var Q0;
            Q0=qCreatedBy(makeId("Top.planeOp"),FACE);
            var sketch = newSketch(context, id + "F88", { "sketchPlane" : qUnion([Q0])});
            skLineSegment(sketch, "E112", {"start": v(175.87, -12.36) * mm, "end": v(175.87, 22.64) * mm});
            skLineSegment(sketch, "E113", {"start": v(174.77, 19.14) * mm, "end": v(174.77, -9.56) * mm});
            skLineSegment(sketch, "E114", {"start": v(174.77, -9.56) * mm, "end": v(172.37, -12.06) * mm});
            skLineSegment(sketch, "E115", {"start": v(172.37, -12.06) * mm, "end": v(172.37, -12.36) * mm});
            skLineSegment(sketch, "E116", {"start": v(172.37, -12.36) * mm, "end": v(175.87, -12.36) * mm});
            skLineSegment(sketch, "E117", {"start": v(174.77, -8.86) * mm, "end": v(174.27, -8.68) * mm});
            skLineSegment(sketch, "E118", {"start": v(174.27, -8.68) * mm, "end": v(174.77, -8.44) * mm});
            skLineSegment(sketch, "E119.0.1.0", {"start": v(174.77, -7.26) * mm, "end": v(174.27, -7.08) * mm});
            skLineSegment(sketch, "E119.0.1.1", {"start": v(174.27, -7.08) * mm, "end": v(174.77, -6.84) * mm});
            skLineSegment(sketch, "E119.0.2.0", {"start": v(174.77, -5.66) * mm, "end": v(174.27, -5.48) * mm});
            skLineSegment(sketch, "E119.0.2.1", {"start": v(174.27, -5.48) * mm, "end": v(174.77, -5.24) * mm});
            skLineSegment(sketch, "E119.0.3.0", {"start": v(174.77, -4.06) * mm, "end": v(174.27, -3.88) * mm});
            skLineSegment(sketch, "E119.0.3.1", {"start": v(174.27, -3.88) * mm, "end": v(174.77, -3.64) * mm});
            skLineSegment(sketch, "E119.0.4.0", {"start": v(174.77, -2.46) * mm, "end": v(174.27, -2.28) * mm});
            skLineSegment(sketch, "E119.0.4.1", {"start": v(174.27, -2.28) * mm, "end": v(174.77, -2.04) * mm});
            skLineSegment(sketch, "E119.0.5.0", {"start": v(174.77, -0.86) * mm, "end": v(174.27, -0.68) * mm});
            skLineSegment(sketch, "E119.0.5.1", {"start": v(174.27, -0.68) * mm, "end": v(174.77, -0.44) * mm});
            skLineSegment(sketch, "E119.0.6.0", {"start": v(174.77, 0.74) * mm, "end": v(174.27, 0.92) * mm});
            skLineSegment(sketch, "E119.0.6.1", {"start": v(174.27, 0.92) * mm, "end": v(174.77, 1.16) * mm});
            skLineSegment(sketch, "E119.0.7.0", {"start": v(174.77, 2.34) * mm, "end": v(174.27, 2.52) * mm});
            skLineSegment(sketch, "E119.0.7.1", {"start": v(174.27, 2.52) * mm, "end": v(174.77, 2.76) * mm});
            skLineSegment(sketch, "E119.0.8.0", {"start": v(174.77, 3.94) * mm, "end": v(174.27, 4.12) * mm});
            skLineSegment(sketch, "E119.0.8.1", {"start": v(174.27, 4.12) * mm, "end": v(174.77, 4.36) * mm});
            skLineSegment(sketch, "E119.0.9.0", {"start": v(174.77, 5.54) * mm, "end": v(174.27, 5.72) * mm});
            skLineSegment(sketch, "E119.0.9.1", {"start": v(174.27, 5.72) * mm, "end": v(174.77, 5.96) * mm});
            skLineSegment(sketch, "E119.0.10.0", {"start": v(174.77, 7.14) * mm, "end": v(174.27, 7.32) * mm});
            skLineSegment(sketch, "E119.0.10.1", {"start": v(174.27, 7.32) * mm, "end": v(174.77, 7.56) * mm});
            skLineSegment(sketch, "E119.0.11.0", {"start": v(174.77, 8.74) * mm, "end": v(174.27, 8.92) * mm});
            skLineSegment(sketch, "E119.0.11.1", {"start": v(174.27, 8.92) * mm, "end": v(174.77, 9.16) * mm});
            skLineSegment(sketch, "E119.0.12.0", {"start": v(174.77, 10.34) * mm, "end": v(174.27, 10.52) * mm});
            skLineSegment(sketch, "E119.0.12.1", {"start": v(174.27, 10.52) * mm, "end": v(174.77, 10.76) * mm});
            skLineSegment(sketch, "E119.0.13.0", {"start": v(174.77, 11.94) * mm, "end": v(174.27, 12.12) * mm});
            skLineSegment(sketch, "E119.0.13.1", {"start": v(174.27, 12.12) * mm, "end": v(174.77, 12.36) * mm});
            skLineSegment(sketch, "E119.0.14.0", {"start": v(174.77, 13.54) * mm, "end": v(174.27, 13.72) * mm});
            skLineSegment(sketch, "E119.0.14.1", {"start": v(174.27, 13.72) * mm, "end": v(174.77, 13.96) * mm});
            skLineSegment(sketch, "E119.0.15.0", {"start": v(174.77, 15.14) * mm, "end": v(174.27, 15.32) * mm});
            skLineSegment(sketch, "E119.0.15.1", {"start": v(174.27, 15.32) * mm, "end": v(174.77, 15.56) * mm});
            skLineSegment(sketch, "E119.0.16.0", {"start": v(174.77, 16.74) * mm, "end": v(174.27, 16.92) * mm});
            skLineSegment(sketch, "E119.0.16.1", {"start": v(174.27, 16.92) * mm, "end": v(174.77, 17.16) * mm});
            skLineSegment(sketch, "E119.0.17.0", {"start": v(174.77, 18.34) * mm, "end": v(174.27, 18.52) * mm});
            skLineSegment(sketch, "E119.0.17.1", {"start": v(174.27, 18.52) * mm, "end": v(174.77, 18.76) * mm});
            skLineSegment(sketch, "E119.direction1", {"start": v(174.27, -8.68) * mm, "end": v(199.27, -8.68) * mm, "construction": true});
            skLineSegment(sketch, "E119.direction2", {"start": v(174.27, -8.68) * mm, "end": v(174.27, -7.08) * mm, "construction": true});
            skLineSegment(sketch, "E120", {"start": v(175.87, 22.64) * mm, "end": v(174.77, 19.14) * mm});
            skSolve(sketch);
        }
        {
            var Q0;
            Q0=qSketchRegion(id+"F88",true);
            var Q1;
            Q1=sQuery(id+"F88.wireOp",EDGE,"E112");
            revolve(context, id + "F89", {"surfaceOperationType" : NewSurfaceOperationType.NEW, "entities" : qUnion([Q0]), "axis" : qUnion([Q1]), "revolveType" : RevolveType.FULL});
        }
        {
            var Q0;
            Q0=makeQuery(id+"F89.opRevolve","SWEPT_FACE",FACE,{"disambiguationData":[OSD([sQuery(id+"F88.wireOp",EDGE,"E116")])]});
            var sketch = newSketch(context, id + "F90", { "sketchPlane" : qUnion([Q0])});
            skLineSegment(sketch, "E121.bottom", {"start": v(173.42, 0.45) * mm, "end": v(175.42, 0.45) * mm});
            skLineSegment(sketch, "E121.top", {"start": v(173.42, -0.45) * mm, "end": v(175.42, -0.45) * mm});
            skLineSegment(sketch, "E121.left", {"start": v(173.42, 0.45) * mm, "end": v(173.42, -0.45) * mm});
            skLineSegment(sketch, "E121.right", {"start": v(178.42, 0.45) * mm, "end": v(178.42, -0.45) * mm});
            skLineSegment(sketch, "E122.bottom", {"start": v(175.42, 2.55) * mm, "end": v(176.32, 2.55) * mm});
            skLineSegment(sketch, "E122.top", {"start": v(175.42, -2.36) * mm, "end": v(176.32, -2.36) * mm});
            skLineSegment(sketch, "E122.left", {"start": v(175.42, 2.55) * mm, "end": v(175.42, 0.45) * mm});
            skLineSegment(sketch, "E123", {"start": v(175.87, 0) * mm, "end": v(178.42, 0) * mm, "construction": true});
            skLineSegment(sketch, "E124", {"start": v(175.87, 0) * mm, "end": v(175.87, 2.55) * mm, "construction": true});
            skLineSegment(sketch, "E125.trimOffspring", {"start": v(176.32, 0.45) * mm, "end": v(178.42, 0.45) * mm});
            skLineSegment(sketch, "E126.trimOffspring", {"start": v(176.32, -0.45) * mm, "end": v(178.42, -0.45) * mm});
            skLineSegment(sketch, "E127.trimOffspring", {"start": v(176.32, -0.45) * mm, "end": v(176.32, -2.36) * mm});
            skLineSegment(sketch, "E128.trimOffspring", {"start": v(175.42, -0.45) * mm, "end": v(175.42, -2.36) * mm});
            skLineSegment(sketch, "E129", {"start": v(176.32, 0.45) * mm, "end": v(176.32, 2.55) * mm});
            skSolve(sketch);
        }
        {
            var Q0;
            Q0=qSketchRegion(id+"F90",true);
            extrude(context, id + "F91", {"entities" : qUnion([Q0]), "operationType" : NewBodyOperationType.REMOVE, "oppositeDirection" : true, "depth" : 0.2 * mm, "offsetDistance" : 25 * mm});
        }
        {
            var Q0;
            Q0=makeQuery(id+"F66.opExtrude","CAP_FACE",FACE,{"disambiguationData":[OSD([sQuery(id+"F65.wireOp",EDGE,"E85"),sQuery(id+"F65.wireOp",EDGE,"E86")])],"isStart":false});
            var sketch = newSketch(context, id + "F92", { "sketchPlane" : qUnion([Q0])});
            skCircle(sketch, "E130", {"center": v(-28.96, -24.67) * mm, "radius": 2.15 * mm});
            skCircle(sketch, "E131", {"center": v(-28.96, -24.67) * mm, "radius": 6 * mm});
            skSolve(sketch);
        }
        {
            var Q0;
            Q0=qSketchRegion(id+"F92",true);
            extrude(context, id + "F93", {"entities" : qUnion([Q0]), "depth" : 1.2 * mm, "offsetDistance" : 25 * mm});
        }
        {
            var Q0;
            Q0=qCreatedBy(makeId("Top.planeOp"),FACE);
            var sketch = newSketch(context, id + "F94", { "sketchPlane" : qUnion([Q0])});
            skLineSegment(sketch, "E132", {"start": v(72.26, 70.64) * mm, "end": v(72.26, 27.89) * mm});
            skLineSegment(sketch, "E133", {"start": v(72.26, 27.89) * mm, "end": v(70.16, 27.89) * mm});
            skLineSegment(sketch, "E134", {"start": v(67.5, 30.04) * mm, "end": v(67.5, 30.64) * mm});
            skLineSegment(sketch, "E135", {"start": v(67.5, 30.64) * mm, "end": v(69.76, 30.64) * mm});
            skLineSegment(sketch, "E136", {"start": v(69.76, 30.64) * mm, "end": v(69.76, 70.24) * mm});
            skLineSegment(sketch, "E137", {"start": v(69.76, 70.24) * mm, "end": v(70.12, 70.64) * mm});
            skLineSegment(sketch, "E138", {"start": v(70.12, 70.64) * mm, "end": v(72.26, 70.64) * mm});
            skArc(sketch, "E139", {"start": v(70.16, 27.89) * mm, "mid": v(68.56, 28.63) * mm, "end": v(67.5, 30.04) * mm});
            skSolve(sketch);
        }
        {
            var Q0;
            Q0 = qSketchRegion(id + "F94", true);
            var Q1;
            Q1=sQuery(id+"F94.wireOp",EDGE,"E132");
            revolve(context, id + "F95", {"surfaceOperationType" : NewSurfaceOperationType.NEW, "entities" : qUnion([Q0]), "axis" : qUnion([Q1]), "revolveType" : RevolveType.FULL});
        }
        {
            var Q0;
            Q0=makeQuery(id+"F95.opRevolve","SWEPT_FACE",FACE,{"disambiguationData":[OSD([sQuery(id+"F94.wireOp",EDGE,"E133")])]});
            var sketch = newSketch(context, id + "F96", { "sketchPlane" : qUnion([Q0])});
            skCircle(sketch, "E140.cCircle", {"center": v(72.26, 0) * mm, "radius": 1.5 * mm, "construction": true});
            skLineSegment(sketch, "E140.0", {"start": v(72.93, 1.6) * mm, "end": v(73.98, 0.21) * mm});
            skLineSegment(sketch, "E140.1", {"start": v(73.98, 0.21) * mm, "end": v(73.3, -1.38) * mm});
            skLineSegment(sketch, "E140.2", {"start": v(73.3, -1.38) * mm, "end": v(71.58, -1.6) * mm});
            skLineSegment(sketch, "E140.3", {"start": v(71.58, -1.6) * mm, "end": v(70.54, -0.21) * mm});
            skLineSegment(sketch, "E140.4", {"start": v(70.54, -0.21) * mm, "end": v(71.21, 1.38) * mm});
            skLineSegment(sketch, "E140.5", {"start": v(71.21, 1.38) * mm, "end": v(72.93, 1.6) * mm});
            skPoint(sketch, "E140.0.midPoint", {"position": v(73.45, 0.9) * mm});
            skSolve(sketch);
        }
        {
            var Q0;
            Q0 = qSketchRegion(id + "F96", true);
            extrude(context, id + "F97", {"entities" : qUnion([Q0]), "operationType" : NewBodyOperationType.REMOVE, "oppositeDirection" : true, "depth" : 2 * mm, "offsetDistance" : 25 * mm});
        }
        {
            var Q0;
            Q0=qCreatedBy(makeId("Front.planeOp"),FACE);
            var sketch = newSketch(context, id + "F98", { "sketchPlane" : qUnion([Q0])});
            skCircle(sketch, "E141", {"center": v(-49.4, -23.93) * mm, "radius": 2.65 * mm});
            skCircle(sketch, "E142", {"center": v(-49.4, -23.93) * mm, "radius": 7.5 * mm});
            skSolve(sketch);
        }
        {
            var Q0;
            Q0 = qSketchRegion(id + "F98", true);
            extrude(context, id + "F99", {"entities" : qUnion([Q0]), "depth" : 1.6 * mm, "offsetDistance" : 25 * mm});
        }
        {
            var Q0;
            Q0=qCreatedBy(makeId("Top.planeOp"),FACE);
            var sketch = newSketch(context, id + "F100", { "sketchPlane" : qUnion([Q0])});
            skLineSegment(sketch, "E143", {"start": v(72.32, 131.6) * mm, "end": v(72.32, 83.84) * mm});
            skLineSegment(sketch, "E144", {"start": v(72.32, 83.84) * mm, "end": v(70.22, 83.84) * mm});
            skLineSegment(sketch, "E145", {"start": v(67.57, 86) * mm, "end": v(67.57, 86.6) * mm});
            skLineSegment(sketch, "E146", {"start": v(67.57, 86.6) * mm, "end": v(69.82, 86.6) * mm});
            skLineSegment(sketch, "E147", {"start": v(69.82, 86.6) * mm, "end": v(69.82, 131.2) * mm});
            skLineSegment(sketch, "E148", {"start": v(69.82, 131.2) * mm, "end": v(70.18, 131.6) * mm});
            skLineSegment(sketch, "E149", {"start": v(70.18, 131.6) * mm, "end": v(72.32, 131.6) * mm});
            skArc(sketch, "E150", {"start": v(70.22, 83.84) * mm, "mid": v(68.63, 84.59) * mm, "end": v(67.57, 86) * mm});
            skSolve(sketch);
        }
        {
            var Q0;
            Q0 = qSketchRegion(id + "F100", true);
            var Q1;
            Q1=sQuery(id+"F100.wireOp",EDGE,"E143");
            revolve(context, id + "F101", {"surfaceOperationType" : NewSurfaceOperationType.NEW, "entities" : qUnion([Q0]), "axis" : qUnion([Q1]), "revolveType" : RevolveType.FULL});
        }
        {
            var Q0;
            Q0=makeQuery(id+"F101.opRevolve","SWEPT_FACE",FACE,{"disambiguationData":[OSD([sQuery(id+"F100.wireOp",EDGE,"E144")])]});
            var sketch = newSketch(context, id + "F102", { "sketchPlane" : qUnion([Q0])});
            skCircle(sketch, "E151.cCircle", {"center": v(72.32, 0) * mm, "radius": 1.5 * mm, "construction": true});
            skLineSegment(sketch, "E151.0", {"start": v(73.82, 0.87) * mm, "end": v(73.82, -0.87) * mm});
            skLineSegment(sketch, "E151.1", {"start": v(73.82, -0.87) * mm, "end": v(72.32, -1.73) * mm});
            skLineSegment(sketch, "E151.2", {"start": v(72.32, -1.73) * mm, "end": v(70.82, -0.87) * mm});
            skLineSegment(sketch, "E151.3", {"start": v(70.82, -0.87) * mm, "end": v(70.82, 0.87) * mm});
            skLineSegment(sketch, "E151.4", {"start": v(70.82, 0.87) * mm, "end": v(72.32, 1.73) * mm});
            skLineSegment(sketch, "E151.5", {"start": v(72.32, 1.73) * mm, "end": v(73.82, 0.87) * mm});
            skPoint(sketch, "E151.0.midPoint", {"position": v(73.82, 0) * mm});
            skSolve(sketch);
        }
        {
            var Q0;
            Q0 = qSketchRegion(id + "F102", true);
            extrude(context, id + "F103", {"entities" : qUnion([Q0]), "operationType" : NewBodyOperationType.REMOVE, "oppositeDirection" : true, "depth" : 2 * mm, "offsetDistance" : 25 * mm});
        }
        {
            var Q0;
            Q0=qCreatedBy(makeId("Top.planeOp"),FACE);
            var sketch = newSketch(context, id + "F104", { "sketchPlane" : qUnion([Q0])});
            skLineSegment(sketch, "E152.bottom", {"start": v(100.97, 17.1) * mm, "end": v(102.72, 17.1) * mm});
            skLineSegment(sketch, "E152.top", {"start": v(101.25, 12.1) * mm, "end": v(105.22, 12.1) * mm});
            skLineSegment(sketch, "E152.left", {"start": v(100.97, 17.1) * mm, "end": v(100.97, 12.39) * mm});
            skLineSegment(sketch, "E152.right", {"start": v(105.22, 17.1) * mm, "end": v(105.22, 12.1) * mm});
            skLineSegment(sketch, "E153.top", {"start": v(105.22, 67.1) * mm, "end": v(103, 67.1) * mm});
            skLineSegment(sketch, "E153.left", {"start": v(105.22, 17.1) * mm, "end": v(105.22, 67.1) * mm});
            skLineSegment(sketch, "E153.right", {"start": v(102.72, 17.1) * mm, "end": v(102.72, 66.82) * mm});
            skLineSegment(sketch, "E154", {"start": v(100.97, 12.39) * mm, "end": v(101.25, 12.1) * mm});
            skLineSegment(sketch, "E155", {"start": v(102.72, 66.82) * mm, "end": v(103, 67.1) * mm});
            skSolve(sketch);
        }
        {
            var Q0;
            Q0 = qSketchRegion(id + "F104", true);
            var Q1;
            Q1=sQuery(id+"F104.wireOp",EDGE,"E153.left");
            revolve(context, id + "F105", {"surfaceOperationType" : NewSurfaceOperationType.NEW, "entities" : qUnion([Q0]), "axis" : qUnion([Q1]), "revolveType" : RevolveType.FULL});
        }
        {
            var Q0;
            Q0=makeQuery(id+"F105.opRevolve","SWEPT_FACE",FACE,{"disambiguationData":[OSD([sQuery(id+"F104.wireOp",EDGE,"E152.top")])]});
            var sketch = newSketch(context, id + "F106", { "sketchPlane" : qUnion([Q0])});
            skCircle(sketch, "E156.cCircle", {"center": v(105.22, 0) * mm, "radius": 2 * mm, "construction": true});
            skLineSegment(sketch, "E156.0", {"start": v(104.9, 2.29) * mm, "end": v(107.04, 1.41) * mm});
            skLineSegment(sketch, "E156.1", {"start": v(107.04, 1.41) * mm, "end": v(107.35, -0.88) * mm});
            skLineSegment(sketch, "E156.2", {"start": v(107.35, -0.88) * mm, "end": v(105.53, -2.29) * mm});
            skLineSegment(sketch, "E156.3", {"start": v(105.53, -2.29) * mm, "end": v(103.39, -1.41) * mm});
            skLineSegment(sketch, "E156.4", {"start": v(103.39, -1.41) * mm, "end": v(103.08, 0.88) * mm});
            skLineSegment(sketch, "E156.5", {"start": v(103.08, 0.88) * mm, "end": v(104.9, 2.29) * mm});
            skPoint(sketch, "E156.0.midPoint", {"position": v(105.98, 1.85) * mm});
            skSolve(sketch);
        }
        {
            var Q0;
            Q0 = qSketchRegion(id + "F106", true);
            extrude(context, id + "F107", {"entities" : qUnion([Q0]), "operationType" : NewBodyOperationType.REMOVE, "oppositeDirection" : true, "depth" : 3 * mm, "offsetDistance" : 25 * mm});
        }
        {
            var Q0;
            Q0=qCreatedBy(makeId("Front.planeOp"),FACE);
            var sketch = newSketch(context, id + "F108", { "sketchPlane" : qUnion([Q0])});
            skArc(sketch, "E157", {"start": v(-48.02, 16.46) * mm, "mid": v(-46.9, 12.25) * mm, "end": v(-43.83, 9.14) * mm});
            skCircle(sketch, "E158", {"center": v(-39.52, 16.46) * mm, "radius": 2.5 * mm});
            skLineSegment(sketch, "E159", {"start": v(-39.52, 24.96) * mm, "end": v(-39.52, 18.96) * mm});
            skLineSegment(sketch, "E160", {"start": v(-48.02, 16.46) * mm, "end": v(-42.02, 16.46) * mm});
            skLineSegment(sketch, "E161", {"start": v(-46.84, 16.46) * mm, "end": v(-46.84, 20.78) * mm});
            skLineSegment(sketch, "E162", {"start": v(-39.52, 23.79) * mm, "end": v(-35.2, 23.79) * mm});
            skLineSegment(sketch, "E163", {"start": v(-32.2, 16.46) * mm, "end": v(-32.2, 12.15) * mm});
            skLineSegment(sketch, "E164", {"start": v(-39.52, 9.14) * mm, "end": v(-43.83, 9.14) * mm});
            skArc(sketch, "E165.trimOffspring", {"start": v(-39.52, 7.96) * mm, "mid": v(-35.3, 9.08) * mm, "end": v(-32.2, 12.15) * mm});
            skArc(sketch, "E166.trimOffspring", {"start": v(-31.02, 16.46) * mm, "mid": v(-32.14, 20.68) * mm, "end": v(-35.2, 23.79) * mm});
            skArc(sketch, "E167.trimOffspring", {"start": v(-39.52, 24.96) * mm, "mid": v(-43.74, 23.84) * mm, "end": v(-46.84, 20.78) * mm});
            skLineSegment(sketch, "E168.trimOffspring", {"start": v(-39.52, 13.96) * mm, "end": v(-39.52, 7.96) * mm});
            skLineSegment(sketch, "E169.trimOffspring", {"start": v(-37.02, 16.46) * mm, "end": v(-31.02, 16.46) * mm});
            skSolve(sketch);
        }
        {
            var Q0;
            Q0 = qSketchRegion(id + "F108", true);
            extrude(context, id + "F109", {"entities" : qUnion([Q0]), "depth" : 1.2 * mm, "offsetDistance" : 25 * mm});
        }
        {
            var Q0;
            Q0=makeQuery(id+"F109.opExtrude","CAP_FACE",FACE,{"disambiguationData":[OSD([sQuery(id+"F108.wireOp",EDGE,"E157"),sQuery(id+"F108.wireOp",EDGE,"E158")])],"isStart":true});
            var sketch = newSketch(context, id + "F110", { "sketchPlane" : qUnion([Q0])});
            skCircle(sketch, "E170", {"center": v(39.52, 16.46) * mm, "radius": 2.5 * mm});
            skCircle(sketch, "E171", {"center": v(39.52, 16.46) * mm, "radius": 3.25 * mm});
            skSolve(sketch);
        }
        {
            var Q0;
            Q0 = qSketchRegion(id + "F110", true);
            extrude(context, id + "F111", {"entities" : qUnion([Q0]), "operationType" : NewBodyOperationType.ADD, "depth" : 8 * mm, "offsetDistance" : 25 * mm});
        }
        {
            var Q0;
            Q0=makeQuery(id+"F109.opExtrude","CAP_FACE",FACE,{"disambiguationData":[OSD([sQuery(id+"F108.wireOp",EDGE,"E157"),sQuery(id+"F108.wireOp",EDGE,"E158"),sQuery(id+"F108.wireOp",EDGE,"E159"),sQuery(id+"F108.wireOp",EDGE,"E160"),sQuery(id+"F108.wireOp",EDGE,"E161"),sQuery(id+"F108.wireOp",EDGE,"E162"),sQuery(id+"F108.wireOp",EDGE,"E163"),sQuery(id+"F108.wireOp",EDGE,"E164"),sQuery(id+"F108.wireOp",EDGE,"E165.trimOffspring"),sQuery(id+"F108.wireOp",EDGE,"E166.trimOffspring"),sQuery(id+"F108.wireOp",EDGE,"E167.trimOffspring"),sQuery(id+"F108.wireOp",EDGE,"E168.trimOffspring"),sQuery(id+"F108.wireOp",EDGE,"E169.trimOffspring")])],"isStart":true});
            var sketch = newSketch(context, id + "F112", { "sketchPlane" : qUnion([Q0])});
            skLineSegment(sketch, "E172", {"start": v(39.52, 24.96) * mm, "end": v(39.52, 23.79) * mm});
            skLineSegment(sketch, "E173", {"start": v(39.52, 23.79) * mm, "end": v(40.72, 23.79) * mm});
            skLineSegment(sketch, "E174", {"start": v(40.72, 23.79) * mm, "end": v(40.72, 24.88) * mm});
            skArc(sketch, "E175.0", {"start": v(39.52, 24.96) * mm, "mid": v(40.12, 24.94) * mm, "end": v(40.72, 24.88) * mm});
            skLineSegment(sketch, "E176.1.0", {"start": v(32.2, 16.46) * mm, "end": v(32.2, 17.66) * mm});
            skLineSegment(sketch, "E176.1.1", {"start": v(31.02, 16.46) * mm, "end": v(32.2, 16.46) * mm});
            skLineSegment(sketch, "E176.1.2", {"start": v(32.2, 17.66) * mm, "end": v(31.1, 17.66) * mm});
            skArc(sketch, "E176.1.3", {"start": v(31.02, 16.46) * mm, "mid": v(31.04, 17.07) * mm, "end": v(31.1, 17.66) * mm});
            skLineSegment(sketch, "E176.2.0", {"start": v(39.52, 9.14) * mm, "end": v(38.32, 9.14) * mm});
            skLineSegment(sketch, "E176.2.1", {"start": v(39.52, 7.96) * mm, "end": v(39.52, 9.14) * mm});
            skLineSegment(sketch, "E176.2.2", {"start": v(38.32, 9.14) * mm, "end": v(38.32, 8.05) * mm});
            skArc(sketch, "E176.2.3", {"start": v(39.52, 7.96) * mm, "mid": v(38.92, 7.99) * mm, "end": v(38.32, 8.05) * mm});
            skLineSegment(sketch, "E176.3.0", {"start": v(46.84, 16.46) * mm, "end": v(46.84, 15.26) * mm});
            skLineSegment(sketch, "E176.3.1", {"start": v(48.02, 16.46) * mm, "end": v(46.84, 16.46) * mm});
            skLineSegment(sketch, "E176.3.2", {"start": v(46.84, 15.26) * mm, "end": v(47.93, 15.26) * mm});
            skArc(sketch, "E176.3.3", {"start": v(48.02, 16.46) * mm, "mid": v(48, 15.86) * mm, "end": v(47.93, 15.26) * mm});
            skSolve(sketch);
        }
        {
            var Q0;
            Q0 = qSketchRegion(id + "F112", true);
            var Q1;
            Q1 = qConstructionFilter(qBodyType(qCreatedBy(id + "F112" ,EDGE), BodyType.WIRE), ConstructionObject.NO);
            extrude(context, id + "F113", {"entities" : qUnion([Q0]), "operationType" : NewBodyOperationType.ADD, "surfaceEntities" : qUnion([Q1]), "depth" : 4 * mm, "offsetDistance" : 25 * mm, "hasDraft" : true, "draftAngle" : 5 * degree, "draftPullDirection" : true});
        }
        {
            var Q0;
            Q0=qCreatedBy(makeId("Top.planeOp"),FACE);
            var sketch = newSketch(context, id + "F114", { "sketchPlane" : qUnion([Q0])});
            skLineSegment(sketch, "E177", {"start": v(93.34, 116.93) * mm, "end": v(93.34, 84.18) * mm});
            skLineSegment(sketch, "E178", {"start": v(93.34, 84.18) * mm, "end": v(91.24, 84.18) * mm});
            skLineSegment(sketch, "E179", {"start": v(88.59, 86.33) * mm, "end": v(88.59, 86.93) * mm});
            skLineSegment(sketch, "E180", {"start": v(88.59, 86.93) * mm, "end": v(90.84, 86.93) * mm});
            skLineSegment(sketch, "E181", {"start": v(90.84, 86.93) * mm, "end": v(90.84, 116.53) * mm});
            skLineSegment(sketch, "E182", {"start": v(90.84, 116.53) * mm, "end": v(91.2, 116.93) * mm});
            skLineSegment(sketch, "E183", {"start": v(91.2, 116.93) * mm, "end": v(93.34, 116.93) * mm});
            skArc(sketch, "E184", {"start": v(91.24, 84.18) * mm, "mid": v(89.65, 84.92) * mm, "end": v(88.59, 86.33) * mm});
            skSolve(sketch);
        }
        {
            var Q0;
            Q0 = qSketchRegion(id + "F114", true);
            var Q1;
            Q1=sQuery(id+"F114.wireOp",EDGE,"E177");
            revolve(context, id + "F115", {"surfaceOperationType" : NewSurfaceOperationType.NEW, "entities" : qUnion([Q0]), "axis" : qUnion([Q1]), "revolveType" : RevolveType.FULL});
        }
        {
            var Q0;
            Q0=makeQuery(id+"F115.opRevolve","SWEPT_FACE",FACE,{"disambiguationData":[OSD([sQuery(id+"F114.wireOp",EDGE,"E178")])]});
            var sketch = newSketch(context, id + "F116", { "sketchPlane" : qUnion([Q0])});
            skCircle(sketch, "E185.cCircle", {"center": v(93.34, 0) * mm, "radius": 1.5 * mm, "construction": true});
            skLineSegment(sketch, "E185.0", {"start": v(95.07, 0.06) * mm, "end": v(94.25, -1.47) * mm});
            skLineSegment(sketch, "E185.1", {"start": v(94.25, -1.47) * mm, "end": v(92.52, -1.53) * mm});
            skLineSegment(sketch, "E185.2", {"start": v(92.52, -1.53) * mm, "end": v(91.6, -0.06) * mm});
            skLineSegment(sketch, "E185.3", {"start": v(91.6, -0.06) * mm, "end": v(92.43, 1.47) * mm});
            skLineSegment(sketch, "E185.4", {"start": v(92.43, 1.47) * mm, "end": v(94.16, 1.53) * mm});
            skLineSegment(sketch, "E185.5", {"start": v(94.16, 1.53) * mm, "end": v(95.07, 0.06) * mm});
            skPoint(sketch, "E185.0.midPoint", {"position": v(94.66, -0.7) * mm});
            skSolve(sketch);
        }
        {
            var Q0;
            Q0 = qSketchRegion(id + "F116", true);
            extrude(context, id + "F117", {"entities" : qUnion([Q0]), "operationType" : NewBodyOperationType.REMOVE, "oppositeDirection" : true, "depth" : 2 * mm, "offsetDistance" : 25 * mm});
        }
        {
            var Q0;
            Q0=qCreatedBy(makeId("Top.planeOp"),FACE);
            var sketch = newSketch(context, id + "F118", { "sketchPlane" : qUnion([Q0])});
            skLineSegment(sketch, "E186", {"start": v(109.7, 114.58) * mm, "end": v(109.7, 76.83) * mm});
            skLineSegment(sketch, "E187", {"start": v(109.7, 76.83) * mm, "end": v(107.6, 76.83) * mm});
            skLineSegment(sketch, "E188", {"start": v(104.95, 78.98) * mm, "end": v(104.95, 79.58) * mm});
            skLineSegment(sketch, "E189", {"start": v(104.95, 79.58) * mm, "end": v(107.2, 79.58) * mm});
            skLineSegment(sketch, "E190", {"start": v(107.2, 79.58) * mm, "end": v(107.2, 114.19) * mm});
            skLineSegment(sketch, "E191", {"start": v(107.2, 114.19) * mm, "end": v(107.56, 114.58) * mm});
            skLineSegment(sketch, "E192", {"start": v(107.56, 114.58) * mm, "end": v(109.7, 114.58) * mm});
            skArc(sketch, "E193", {"start": v(107.6, 76.83) * mm, "mid": v(106, 77.58) * mm, "end": v(104.95, 78.98) * mm});
            skSolve(sketch);
        }
        {
            var Q0;
            Q0 = qSketchRegion(id + "F118", true);
            var Q1;
            Q1=sQuery(id+"F118.wireOp",EDGE,"E186");
            revolve(context, id + "F119", {"surfaceOperationType" : NewSurfaceOperationType.NEW, "entities" : qUnion([Q0]), "axis" : qUnion([Q1]), "revolveType" : RevolveType.FULL});
        }
        {
            var Q0;
            Q0=makeQuery(id+"F119.opRevolve","SWEPT_FACE",FACE,{"disambiguationData":[OSD([sQuery(id+"F118.wireOp",EDGE,"E187")])]});
            var sketch = newSketch(context, id + "F120", { "sketchPlane" : qUnion([Q0])});
            skCircle(sketch, "E194.cCircle", {"center": v(109.7, 0) * mm, "radius": 1.5 * mm, "construction": true});
            skLineSegment(sketch, "E194.0", {"start": v(110.06, 1.7) * mm, "end": v(111.35, 0.53) * mm});
            skLineSegment(sketch, "E194.1", {"start": v(111.35, 0.53) * mm, "end": v(110.98, -1.16) * mm});
            skLineSegment(sketch, "E194.2", {"start": v(110.98, -1.16) * mm, "end": v(109.34, -1.7) * mm});
            skLineSegment(sketch, "E194.3", {"start": v(109.34, -1.7) * mm, "end": v(108.05, -0.53) * mm});
            skLineSegment(sketch, "E194.4", {"start": v(108.05, -0.53) * mm, "end": v(108.41, 1.16) * mm});
            skLineSegment(sketch, "E194.5", {"start": v(108.41, 1.16) * mm, "end": v(110.06, 1.7) * mm});
            skPoint(sketch, "E194.0.midPoint", {"position": v(110.7, 1.11) * mm});
            skSolve(sketch);
        }
        {
            var Q0;
            Q0 = qSketchRegion(id + "F120", true);
            extrude(context, id + "F121", {"entities" : qUnion([Q0]), "operationType" : NewBodyOperationType.REMOVE, "oppositeDirection" : true, "depth" : 2 * mm, "offsetDistance" : 25 * mm});
        }
        {
            var Q0;
            Q0=qCreatedBy(makeId("Top.planeOp"),FACE);
            var sketch = newSketch(context, id + "F122", { "sketchPlane" : qUnion([Q0])});
            skLineSegment(sketch, "E195.bottom", {"start": v(137.56, 46.12) * mm, "end": v(139.3, 46.12) * mm});
            skLineSegment(sketch, "E195.top", {"start": v(137.84, 41.12) * mm, "end": v(141.8, 41.12) * mm});
            skLineSegment(sketch, "E195.left", {"start": v(137.56, 46.12) * mm, "end": v(137.56, 41.4) * mm});
            skLineSegment(sketch, "E195.right", {"start": v(141.8, 46.12) * mm, "end": v(141.8, 41.12) * mm});
            skLineSegment(sketch, "E196.top", {"start": v(141.8, 101.12) * mm, "end": v(139.59, 101.12) * mm});
            skLineSegment(sketch, "E196.left", {"start": v(141.8, 46.12) * mm, "end": v(141.8, 101.12) * mm});
            skLineSegment(sketch, "E196.right", {"start": v(139.3, 46.12) * mm, "end": v(139.3, 100.84) * mm});
            skLineSegment(sketch, "E197", {"start": v(137.56, 41.4) * mm, "end": v(137.84, 41.12) * mm});
            skLineSegment(sketch, "E198", {"start": v(139.3, 100.84) * mm, "end": v(139.59, 101.12) * mm});
            skSolve(sketch);
        }
        {
            var Q0;
            Q0 = qSketchRegion(id + "F122", true);
            var Q1;
            Q1=sQuery(id+"F122.wireOp",EDGE,"E196.left");
            revolve(context, id + "F123", {"surfaceOperationType" : NewSurfaceOperationType.NEW, "entities" : qUnion([Q0]), "axis" : qUnion([Q1]), "revolveType" : RevolveType.FULL});
        }
        {
            var Q0;
            Q0=makeQuery(id+"F123.opRevolve","SWEPT_FACE",FACE,{"disambiguationData":[OSD([sQuery(id+"F122.wireOp",EDGE,"E195.top")])]});
            var sketch = newSketch(context, id + "F124", { "sketchPlane" : qUnion([Q0])});
            skCircle(sketch, "E199.cCircle", {"center": v(141.8, 0) * mm, "radius": 2 * mm, "construction": true});
            skLineSegment(sketch, "E199.0", {"start": v(144.1, 0.19) * mm, "end": v(143.12, -1.9) * mm});
            skLineSegment(sketch, "E199.1", {"start": v(143.12, -1.9) * mm, "end": v(140.82, -2.09) * mm});
            skLineSegment(sketch, "E199.2", {"start": v(140.82, -2.09) * mm, "end": v(139.5, -0.19) * mm});
            skLineSegment(sketch, "E199.3", {"start": v(139.5, -0.19) * mm, "end": v(140.5, 1.9) * mm});
            skLineSegment(sketch, "E199.4", {"start": v(140.5, 1.9) * mm, "end": v(142.8, 2.09) * mm});
            skLineSegment(sketch, "E199.5", {"start": v(142.8, 2.09) * mm, "end": v(144.1, 0.19) * mm});
            skPoint(sketch, "E199.0.midPoint", {"position": v(143.61, -0.86) * mm});
            skSolve(sketch);
        }
        {
            var Q0;
            Q0 = qSketchRegion(id + "F124", true);
            extrude(context, id + "F125", {"entities" : qUnion([Q0]), "operationType" : NewBodyOperationType.REMOVE, "oppositeDirection" : true, "depth" : 2 * mm, "offsetDistance" : 25 * mm});
        }
        {
            var Q0;
            Q0=qCreatedBy(makeId("Top.planeOp"),FACE);
            var sketch = newSketch(context, id + "F126", { "sketchPlane" : qUnion([Q0])});
            skLineSegment(sketch, "E200.bottom", {"start": v(160.56, 61.43) * mm, "end": v(162.31, 61.43) * mm});
            skLineSegment(sketch, "E200.top", {"start": v(160.85, 56.43) * mm, "end": v(164.81, 56.43) * mm});
            skLineSegment(sketch, "E200.left", {"start": v(160.56, 61.43) * mm, "end": v(160.56, 56.71) * mm});
            skLineSegment(sketch, "E200.right", {"start": v(164.81, 61.43) * mm, "end": v(164.81, 56.43) * mm});
            skLineSegment(sketch, "E201.top", {"start": v(164.81, 101.43) * mm, "end": v(162.6, 101.43) * mm});
            skLineSegment(sketch, "E201.left", {"start": v(164.81, 61.43) * mm, "end": v(164.81, 101.43) * mm});
            skLineSegment(sketch, "E201.right", {"start": v(162.31, 61.43) * mm, "end": v(162.31, 101.15) * mm});
            skLineSegment(sketch, "E202", {"start": v(160.56, 56.71) * mm, "end": v(160.85, 56.43) * mm});
            skLineSegment(sketch, "E203", {"start": v(162.31, 101.15) * mm, "end": v(162.6, 101.43) * mm});
            skSolve(sketch);
        }
        {
            var Q0;
            Q0 = qSketchRegion(id + "F126", true);
            var Q1;
            Q1=sQuery(id+"F126.wireOp",EDGE,"E201.left");
            revolve(context, id + "F127", {"surfaceOperationType" : NewSurfaceOperationType.NEW, "entities" : qUnion([Q0]), "axis" : qUnion([Q1]), "revolveType" : RevolveType.FULL});
        }
        {
            var Q0;
            Q0=makeQuery(id+"F127.opRevolve","SWEPT_FACE",FACE,{"disambiguationData":[OSD([sQuery(id+"F126.wireOp",EDGE,"E200.top")])]});
            var sketch = newSketch(context, id + "F128", { "sketchPlane" : qUnion([Q0])});
            skCircle(sketch, "E204.cCircle", {"center": v(164.81, 0) * mm, "radius": 2 * mm, "construction": true});
            skLineSegment(sketch, "E204.0", {"start": v(166.94, -0.89) * mm, "end": v(165.1, -2.3) * mm});
            skLineSegment(sketch, "E204.1", {"start": v(165.1, -2.3) * mm, "end": v(162.98, -1.4) * mm});
            skLineSegment(sketch, "E204.2", {"start": v(162.98, -1.4) * mm, "end": v(162.68, 0.89) * mm});
            skLineSegment(sketch, "E204.3", {"start": v(162.68, 0.89) * mm, "end": v(164.52, 2.3) * mm});
            skLineSegment(sketch, "E204.4", {"start": v(164.52, 2.3) * mm, "end": v(166.65, 1.4) * mm});
            skLineSegment(sketch, "E204.5", {"start": v(166.65, 1.4) * mm, "end": v(166.94, -0.89) * mm});
            skPoint(sketch, "E204.0.midPoint", {"position": v(166.03, -1.59) * mm});
            skSolve(sketch);
        }
        {
            var Q0;
            Q0 = qSketchRegion(id + "F128", true);
            extrude(context, id + "F129", {"entities" : qUnion([Q0]), "operationType" : NewBodyOperationType.REMOVE, "oppositeDirection" : true, "depth" : 2 * mm, "offsetDistance" : 25 * mm});
        }
    });
